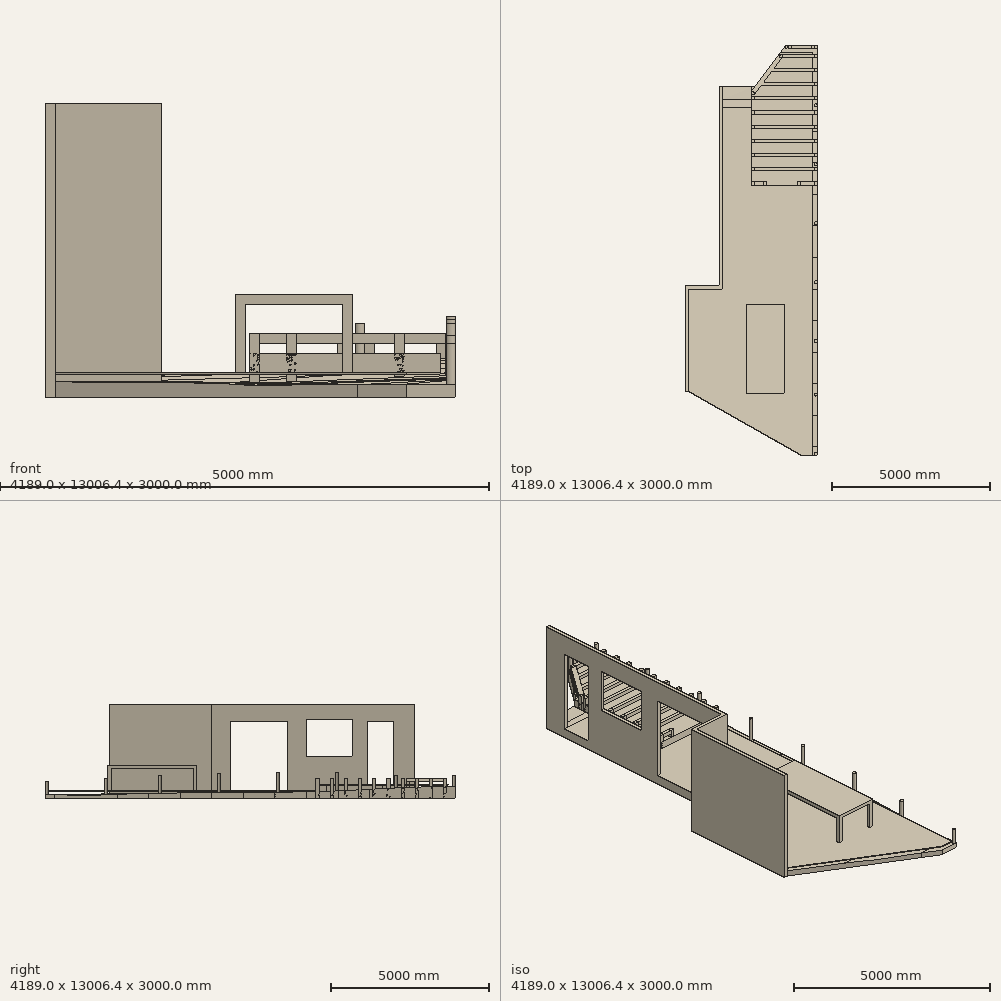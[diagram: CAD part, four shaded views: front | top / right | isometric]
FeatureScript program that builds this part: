
annotation { "Feature Type Name" : "Feature", "Feature Type Description" : "" }
export const myFeature = defineFeature(function(context is Context, id is Id, definition is map)
    precondition{}
    {
        {
            var Q0;
            Q0=qCreatedBy(makeId("Top.planeOp"),FACE);
            var sketch = newSketch(context, id + "F0", { "sketchPlane" : qUnion([Q0])});
            skLineSegment(sketch, "E0", {"start": v(0, 0) * mm, "end": v(0, 6425) * mm});
            skLineSegment(sketch, "E1", {"start": v(0, 0) * mm, "end": v(-1089, 0) * mm});
            skLineSegment(sketch, "E2", {"start": v(-1089, 0) * mm, "end": v(-1089, -3250) * mm});
            skLineSegment(sketch, "E3", {"start": v(-1089, -3250) * mm, "end": v(2495, -5280.43) * mm});
            skLineSegment(sketch, "E4", {"start": v(2495, -5280.43) * mm, "end": v(3000, -5280.43) * mm});
            skLineSegment(sketch, "E5", {"start": v(3000, -5280.43) * mm, "end": v(3000, 7726) * mm});
            skLineSegment(sketch, "E6", {"start": v(0, 6425) * mm, "end": v(1024, 6425) * mm});
            skLineSegment(sketch, "E7", {"start": v(1024, 6425) * mm, "end": v(2000, 7726) * mm});
            skLineSegment(sketch, "E8", {"start": v(2000, 7726) * mm, "end": v(3000, 7726) * mm});
            skPoint(sketch, "E9", {"position": v(1000, 0) * mm});
            skPoint(sketch, "E10", {"position": v(2000, 0) * mm});
            skPoint(sketch, "E11", {"position": v(2000, -1000) * mm});
            skPoint(sketch, "E12", {"position": v(2000, -2000) * mm});
            skPoint(sketch, "E13", {"position": v(2000, -3000) * mm});
            skPoint(sketch, "E14", {"position": v(1000, -1000) * mm});
            skPoint(sketch, "E15", {"position": v(0, -1000) * mm});
            skPoint(sketch, "E16", {"position": v(0, -2000) * mm});
            skPoint(sketch, "E17", {"position": v(1000, -2000) * mm});
            skPoint(sketch, "E18", {"position": v(1000, -3000) * mm});
            skPoint(sketch, "E19", {"position": v(2000, -4000) * mm});
            skPoint(sketch, "E20", {"position": v(1000, 1000) * mm});
            skPoint(sketch, "E21", {"position": v(2000, 1000) * mm});
            skPoint(sketch, "E22", {"position": v(0, 1000) * mm});
            skPoint(sketch, "E23", {"position": v(1000, 2000) * mm});
            skPoint(sketch, "E24", {"position": v(2000, 2000) * mm});
            skPoint(sketch, "E25", {"position": v(1000, 3000) * mm});
            skPoint(sketch, "E26", {"position": v(2000, 3000) * mm});
            skPoint(sketch, "E27", {"position": v(0, 2000) * mm});
            skPoint(sketch, "E28", {"position": v(0, 3000) * mm});
            skPoint(sketch, "E29", {"position": v(1000, 4000) * mm});
            skPoint(sketch, "E30", {"position": v(2000, 4000) * mm});
            skPoint(sketch, "E31", {"position": v(1000, 5000) * mm});
            skPoint(sketch, "E32", {"position": v(2000, 5000) * mm});
            skPoint(sketch, "E33", {"position": v(0, 4000) * mm});
            skPoint(sketch, "E34", {"position": v(0, 5000) * mm});
            skPoint(sketch, "E35", {"position": v(0, 6000) * mm});
            skPoint(sketch, "E36", {"position": v(1000, 6000) * mm});
            skPoint(sketch, "E37", {"position": v(2000, 6000) * mm});
            skPoint(sketch, "E38", {"position": v(-1000, -1000) * mm});
            skPoint(sketch, "E39", {"position": v(-1000, -2000) * mm});
            skPoint(sketch, "E40", {"position": v(-1089, -1000) * mm});
            skPoint(sketch, "E41", {"position": v(-1089, -2000) * mm});
            skPoint(sketch, "E42", {"position": v(-1000, 0) * mm});
            skPoint(sketch, "E43", {"position": v(0, -3000) * mm});
            skPoint(sketch, "E44", {"position": v(-1000, -3000) * mm});
            skPoint(sketch, "E45", {"position": v(-1089, -3000) * mm});
            skPoint(sketch, "E46", {"position": v(1000, -4000) * mm});
            skPoint(sketch, "E47", {"position": v(2000, 7000) * mm});
            skPoint(sketch, "E48", {"position": v(2000, -5000) * mm});
            skPoint(sketch, "E49", {"position": v(-1000, -3300.42) * mm});
            skPoint(sketch, "E50", {"position": v(0, -3866.95) * mm});
            skPoint(sketch, "E51", {"position": v(1000, -4433.47) * mm});
            skPoint(sketch, "E52", {"position": v(3000, -5000) * mm});
            skPoint(sketch, "E53", {"position": v(3000, -4000) * mm});
            skPoint(sketch, "E54", {"position": v(3000, -3000) * mm});
            skPoint(sketch, "E55", {"position": v(3000, -2000) * mm});
            skPoint(sketch, "E56", {"position": v(3000, -1000) * mm});
            skPoint(sketch, "E57", {"position": v(3000, 0) * mm});
            skPoint(sketch, "E58", {"position": v(3000, 1000) * mm});
            skPoint(sketch, "E59", {"position": v(3000, 2000) * mm});
            skPoint(sketch, "E60", {"position": v(3000, 3000) * mm});
            skPoint(sketch, "E61", {"position": v(3000, 4000) * mm});
            skPoint(sketch, "E62", {"position": v(3000, 5000) * mm});
            skPoint(sketch, "E63", {"position": v(3000, 6000) * mm});
            skPoint(sketch, "E64", {"position": v(3000, 7000) * mm});
            skPoint(sketch, "E65", {"position": v(1000, 6425) * mm});
            skPoint(sketch, "E66", {"position": v(2000, -6000) * mm});
            skPoint(sketch, "E67", {"position": v(3000, -6000) * mm});
            skPoint(sketch, "E68", {"position": v(1000, -6000) * mm});
            skPoint(sketch, "E69", {"position": v(0, -6000) * mm});
            skPoint(sketch, "E70", {"position": v(-1000, -6000) * mm});
            skPoint(sketch, "E71", {"position": v(-1089, -6000) * mm});
            skPoint(sketch, "E72", {"position": v(1000, -5000) * mm});
            skPoint(sketch, "E73", {"position": v(0, -5000) * mm});
            skPoint(sketch, "E74", {"position": v(-1000, -5000) * mm});
            skPoint(sketch, "E75", {"position": v(-1089, -5000) * mm});
            skPoint(sketch, "E76", {"position": v(0, -4000) * mm});
            skPoint(sketch, "E77", {"position": v(-1000, -4000) * mm});
            skPoint(sketch, "E78", {"position": v(-1089, -4000) * mm});
            skPoint(sketch, "E79", {"position": v(-1000, 1000) * mm});
            skPoint(sketch, "E80", {"position": v(-1089, 1000) * mm});
            skPoint(sketch, "E81", {"position": v(-1089, 2000) * mm});
            skPoint(sketch, "E82", {"position": v(-1000, 2000) * mm});
            skPoint(sketch, "E83", {"position": v(-1089, 3000) * mm});
            skPoint(sketch, "E84", {"position": v(-1000, 3000) * mm});
            skPoint(sketch, "E85", {"position": v(-1089, 4000) * mm});
            skPoint(sketch, "E86", {"position": v(-1000, 4000) * mm});
            skPoint(sketch, "E87", {"position": v(-1089, 5000) * mm});
            skPoint(sketch, "E88", {"position": v(-1000, 5000) * mm});
            skPoint(sketch, "E89", {"position": v(-1089, 6000) * mm});
            skPoint(sketch, "E90", {"position": v(-1000, 6000) * mm});
            skPoint(sketch, "E91", {"position": v(-1089, 7000) * mm});
            skPoint(sketch, "E92", {"position": v(-1000, 7000) * mm});
            skPoint(sketch, "E93", {"position": v(0, 7000) * mm});
            skPoint(sketch, "E94", {"position": v(0, 8000) * mm});
            skPoint(sketch, "E95", {"position": v(-1000, 8000) * mm});
            skPoint(sketch, "E96", {"position": v(-1089, 8000) * mm});
            skPoint(sketch, "E97", {"position": v(1000, 8000) * mm});
            skPoint(sketch, "E98", {"position": v(2000, 8000) * mm});
            skPoint(sketch, "E99", {"position": v(3000, 8000) * mm});
            skPoint(sketch, "E100", {"position": v(1000, 7000) * mm});
            skSolve(sketch);
        }
        {
            var Q0;
            Q0=qCreatedBy(makeId("Top.planeOp"),FACE);
            cPlane(context, id + "F1", {"entities" : qUnion([Q0]), "cplaneType" : CPlaneType.OFFSET, "offset" : 250 * mm, "oppositeDirection" : true, "width" : 150 * mm, "height" : 150 * mm});
        }
        {
            var Q0;
            Q0=qCreatedBy(id+"F1.planeOp",FACE);
            var sketch = newSketch(context, id + "F2", { "sketchPlane" : qUnion([Q0])});
            skCircle(sketch, "E101", {"center": v(2023.75, 7678.5) * mm, "radius": 47.5 * mm});
            skSolve(sketch);
        }
        {
            var Q0;
            Q0 = qSketchRegion(id + "F2", true);
            extrude(context, id + "F3", {"entities" : qUnion([Q0]), "depth" : 750 * mm, "offsetDistance" : 25 * mm});
        }
        {
            var Q0;
            Q0=qCreatedBy(id+"F1.planeOp",FACE);
            var sketch = newSketch(context, id + "F4", { "sketchPlane" : qUnion([Q0])});
            skCircle(sketch, "E102", {"center": v(2952.5, 7678.5) * mm, "radius": 47.5 * mm});
            skSolve(sketch);
        }
        {
            var Q0;
            Q0 = qSketchRegion(id + "F4", true);
            extrude(context, id + "F5", {"entities" : qUnion([Q0]), "depth" : 750 * mm, "offsetDistance" : 25 * mm});
        }
        {
            var Q0;
            Q0=qCreatedBy(id+"F1.planeOp",FACE);
            var sketch = newSketch(context, id + "F6", { "sketchPlane" : qUnion([Q0])});
            skCircle(sketch, "E103", {"center": v(2952.5, 5831) * mm, "radius": 47.5 * mm});
            skSolve(sketch);
        }
        {
            var Q0;
            Q0 = qSketchRegion(id + "F6", true);
            extrude(context, id + "F7", {"entities" : qUnion([Q0]), "depth" : 750 * mm, "offsetDistance" : 25 * mm});
        }
        {
            var Q0;
            Q0=qCreatedBy(id+"F1.planeOp",FACE);
            var sketch = newSketch(context, id + "F8", { "sketchPlane" : qUnion([Q0])});
            skCircle(sketch, "E104", {"center": v(2952.5, 3956) * mm, "radius": 47.5 * mm});
            skSolve(sketch);
        }
        {
            var Q0;
            Q0 = qSketchRegion(id + "F8", true);
            extrude(context, id + "F9", {"entities" : qUnion([Q0]), "depth" : 820 * mm, "offsetDistance" : 25 * mm});
        }
        {
            var Q0;
            Q0=qCreatedBy(id+"F1.planeOp",FACE);
            var sketch = newSketch(context, id + "F10", { "sketchPlane" : qUnion([Q0])});
            skCircle(sketch, "E105", {"center": v(2952.5, 2092) * mm, "radius": 47.5 * mm});
            skSolve(sketch);
        }
        {
            var Q0;
            Q0 = qSketchRegion(id + "F10", true);
            extrude(context, id + "F11", {"entities" : qUnion([Q0]), "depth" : 830 * mm, "offsetDistance" : 25 * mm});
        }
        {
            var Q0;
            Q0=qCreatedBy(id+"F1.planeOp",FACE);
            var sketch = newSketch(context, id + "F12", { "sketchPlane" : qUnion([Q0])});
            skCircle(sketch, "E106", {"center": v(2952.5, 220) * mm, "radius": 47.5 * mm});
            skSolve(sketch);
        }
        {
            var Q0;
            Q0 = qSketchRegion(id + "F12", true);
            extrude(context, id + "F13", {"entities" : qUnion([Q0]), "depth" : 790 * mm, "offsetDistance" : 25 * mm});
        }
        {
            var Q0;
            Q0=qCreatedBy(id+"F1.planeOp",FACE);
            var sketch = newSketch(context, id + "F14", { "sketchPlane" : qUnion([Q0])});
            skCircle(sketch, "E107", {"center": v(2952.5, -1647) * mm, "radius": 47.5 * mm});
            skSolve(sketch);
        }
        {
            var Q0;
            Q0 = qSketchRegion(id + "F14", true);
            extrude(context, id + "F15", {"entities" : qUnion([Q0]), "depth" : 750 * mm, "offsetDistance" : 25 * mm});
        }
        {
            var Q0;
            Q0=qCreatedBy(id+"F1.planeOp",FACE);
            var sketch = newSketch(context, id + "F16", { "sketchPlane" : qUnion([Q0])});
            skCircle(sketch, "E108", {"center": v(2952.5, -3353) * mm, "radius": 47.5 * mm});
            skSolve(sketch);
        }
        {
            var Q0;
            Q0 = qSketchRegion(id + "F16", true);
            extrude(context, id + "F17", {"entities" : qUnion([Q0]), "depth" : 630 * mm, "offsetDistance" : 25 * mm});
        }
        {
            var Q0;
            Q0=qCreatedBy(id+"F1.planeOp",FACE);
            var sketch = newSketch(context, id + "F18", { "sketchPlane" : qUnion([Q0])});
            skCircle(sketch, "E109", {"center": v(2952.5, -5232.93) * mm, "radius": 47.5 * mm});
            skSolve(sketch);
        }
        {
            var Q0;
            Q0 = qSketchRegion(id + "F18", true);
            extrude(context, id + "F19", {"entities" : qUnion([Q0]), "depth" : 550 * mm, "offsetDistance" : 25 * mm});
        }
        {
            var Q0;
            Q0=sQuery(id+"F0.wireOp",VERTEX,"E94");
            var Q1;
            Q1=qCreatedBy(makeId("Front.planeOp"),FACE);
            cPlane(context, id + "F20", {"entities" : qUnion([Q0, Q1]), "cplaneType" : CPlaneType.PLANE_POINT, "offset" : 25 * mm, "width" : 150 * mm, "height" : 150 * mm});
        }
        {
            var Q0;
            Q0=qCreatedBy(id+"F20.planeOp",FACE);
            var sketch = newSketch(context, id + "F21", { "sketchPlane" : qUnion([Q0])});
            skPoint(sketch, "E110", {"position": v(-1089, -90) * mm});
            skPoint(sketch, "E111", {"position": v(-1000, -90) * mm});
            skPoint(sketch, "E112", {"position": v(0, -1) * mm});
            skPoint(sketch, "E113", {"position": v(1000, 1) * mm});
            skPoint(sketch, "E114", {"position": v(2000, 136) * mm});
            skLineSegment(sketch, "E115", {"start": v(3000, -250) * mm, "end": v(-1089, -250) * mm});
            skLineSegment(sketch, "E116", {"start": v(-1089, -250) * mm, "end": v(-1089, -90) * mm});
            skLineSegment(sketch, "E117", {"start": v(3000, -250) * mm, "end": v(3000, 158) * mm});
            skLineSegment(sketch, "E118", {"start": v(-1089, -90) * mm, "end": v(-1000, -90) * mm});
            skLineSegment(sketch, "E119", {"start": v(-1000, -90) * mm, "end": v(0, -1) * mm});
            skLineSegment(sketch, "E120", {"start": v(0, -1) * mm, "end": v(1000, 1) * mm});
            skFitSpline(sketch, "E121", {"points": [v(3000, 158) * mm, v(2000, 136) * mm, v(1000, 1) * mm], "startDerivative": vector(-253.44, 0) * mm, "endDerivative": vector(-278.02, 0) * mm});
            skSolve(sketch);
        }
        {
            var Q0;
            Q0=sQuery(id+"F0.wireOp",VERTEX,"E93");
            var Q1;
            Q1=qCreatedBy(makeId("Front.planeOp"),FACE);
            cPlane(context, id + "F22", {"entities" : qUnion([Q0, Q1]), "cplaneType" : CPlaneType.PLANE_POINT, "offset" : 25 * mm, "width" : 150 * mm, "height" : 150 * mm});
        }
        {
            var Q0;
            Q0=qCreatedBy(id+"F22.planeOp",FACE);
            var sketch = newSketch(context, id + "F23", { "sketchPlane" : qUnion([Q0])});
            skLineSegment(sketch, "E122", {"start": v(-1089, -90) * mm, "end": v(-1089, -250) * mm});
            skLineSegment(sketch, "E123", {"start": v(-1089, -250) * mm, "end": v(3000, -250) * mm});
            skLineSegment(sketch, "E124", {"start": v(3000, -250) * mm, "end": v(3000, 135) * mm});
            skPoint(sketch, "E125", {"position": v(-1000, -90) * mm});
            skPoint(sketch, "E126", {"position": v(0, -1) * mm});
            skPoint(sketch, "E127", {"position": v(-1000, -2003.57) * mm});
            skPoint(sketch, "E128", {"position": v(1000, 1) * mm});
            skLineSegment(sketch, "E129", {"start": v(-1089, -90) * mm, "end": v(-1000, -90) * mm});
            skLineSegment(sketch, "E130", {"start": v(-1000, -90) * mm, "end": v(0, -1) * mm});
            skLineSegment(sketch, "E131", {"start": v(0, -1) * mm, "end": v(1000, 1) * mm});
            skPoint(sketch, "E132", {"position": v(2000, 87) * mm});
            skFitSpline(sketch, "E133", {"points": [v(3000, 135) * mm, v(2000, 87) * mm, v(1000, 1) * mm], "startDerivative": vector(-235.52, 0) * mm, "endDerivative": vector(-452.7, 6) * mm});
            skSolve(sketch);
        }
        {
            var Q0;
            Q0=qCreatedBy(makeId("Front.planeOp"),FACE);
            var Q1;
            Q1=sQuery(id+"F0.wireOp",VERTEX,"E35");
            cPlane(context, id + "F24", {"entities" : qUnion([Q0, Q1]), "cplaneType" : CPlaneType.PLANE_POINT, "offset" : 25 * mm, "width" : 150 * mm, "height" : 150 * mm});
        }
        {
            var Q0;
            Q0=qCreatedBy(id+"F24.planeOp",FACE);
            var sketch = newSketch(context, id + "F25", { "sketchPlane" : qUnion([Q0])});
            skLineSegment(sketch, "E134", {"start": v(-1089, -90) * mm, "end": v(-1089, -250) * mm});
            skLineSegment(sketch, "E135", {"start": v(-1089, -250) * mm, "end": v(3000, -250) * mm});
            skLineSegment(sketch, "E136", {"start": v(3000, -250) * mm, "end": v(3000, 102) * mm});
            skPoint(sketch, "E137", {"position": v(-1000, -90) * mm});
            skPoint(sketch, "E138", {"position": v(0, -39) * mm});
            skPoint(sketch, "E139", {"position": v(1000, -9) * mm});
            skPoint(sketch, "E140", {"position": v(2000, 38) * mm});
            skLineSegment(sketch, "E141", {"start": v(-1089, -90) * mm, "end": v(-1000, -90) * mm});
            skLineSegment(sketch, "E142", {"start": v(-1000, -90) * mm, "end": v(0, -39) * mm});
            skFitSpline(sketch, "E143", {"points": [v(3000, 102) * mm, v(2000, 38) * mm, v(1000, -9) * mm, v(0, -39) * mm], "startDerivative": vector(-559.95, 0) * mm, "endDerivative": vector(-577.7, 0) * mm});
            skSolve(sketch);
        }
        {
            var Q0;
            Q0=sQuery(id+"F0.wireOp",VERTEX,"E34");
            var Q1;
            Q1=qCreatedBy(makeId("Front.planeOp"),FACE);
            cPlane(context, id + "F26", {"entities" : qUnion([Q0, Q1]), "cplaneType" : CPlaneType.PLANE_POINT, "offset" : 25 * mm, "width" : 150 * mm, "height" : 150 * mm});
        }
        {
            var Q0;
            Q0=qCreatedBy(id+"F26.planeOp",FACE);
            var sketch = newSketch(context, id + "F27", { "sketchPlane" : qUnion([Q0])});
            skLineSegment(sketch, "E144", {"start": v(-1089, -90) * mm, "end": v(-1089, -250) * mm});
            skLineSegment(sketch, "E145", {"start": v(-1089, -250) * mm, "end": v(3000, -250) * mm});
            skLineSegment(sketch, "E146", {"start": v(3000, -250) * mm, "end": v(3000, 50) * mm});
            skLineSegment(sketch, "E147", {"start": v(-1089, -90) * mm, "end": v(-1000, -90) * mm});
            skLineSegment(sketch, "E148", {"start": v(-1000, -90) * mm, "end": v(0, -75) * mm});
            skPoint(sketch, "E149", {"position": v(1000, -51) * mm});
            skPoint(sketch, "E150", {"position": v(2000, -5) * mm});
            skFitSpline(sketch, "E151", {"points": [v(3000, 50) * mm, v(2000, -5) * mm, v(1000, -51) * mm, v(0, -75) * mm], "startDerivative": vector(-368.77, 0) * mm, "endDerivative": vector(-352.57, 0) * mm});
            skSolve(sketch);
        }
        {
            var Q0;
            Q0=sQuery(id+"F0.wireOp",VERTEX,"E33");
            var Q1;
            Q1=qCreatedBy(makeId("Front.planeOp"),FACE);
            cPlane(context, id + "F28", {"entities" : qUnion([Q0, Q1]), "cplaneType" : CPlaneType.PLANE_POINT, "offset" : 25 * mm, "width" : 150 * mm, "height" : 150 * mm});
        }
        {
            var Q0;
            Q0=qCreatedBy(id+"F28.planeOp",FACE);
            var sketch = newSketch(context, id + "F29", { "sketchPlane" : qUnion([Q0])});
            skLineSegment(sketch, "E152", {"start": v(-1089, -90) * mm, "end": v(-1089, -250) * mm});
            skLineSegment(sketch, "E153", {"start": v(-1089, -250) * mm, "end": v(3000, -250) * mm});
            skLineSegment(sketch, "E154", {"start": v(3000, -250) * mm, "end": v(3000, -1) * mm});
            skLineSegment(sketch, "E155", {"start": v(-1089, -90) * mm, "end": v(-1000, -90) * mm});
            skLineSegment(sketch, "E156", {"start": v(-1000, -90) * mm, "end": v(0, -115) * mm});
            skPoint(sketch, "E157", {"position": v(1000, -84) * mm});
            skPoint(sketch, "E158", {"position": v(2000, -11) * mm});
            skFitSpline(sketch, "E159", {"points": [v(3000, -1) * mm, v(2000, -11) * mm, v(1000, -84) * mm, v(0, -115) * mm], "startDerivative": vector(-449.53, 0) * mm, "endDerivative": vector(-406.45, 0) * mm});
            skSolve(sketch);
        }
        {
            var Q0;
            Q0=sQuery(id+"F0.wireOp",VERTEX,"E28");
            var Q1;
            Q1=qCreatedBy(makeId("Front.planeOp"),FACE);
            cPlane(context, id + "F30", {"entities" : qUnion([Q0, Q1]), "cplaneType" : CPlaneType.PLANE_POINT, "offset" : 25 * mm, "width" : 150 * mm, "height" : 150 * mm});
        }
        {
            var Q0;
            Q0=qCreatedBy(id+"F30.planeOp",FACE);
            var sketch = newSketch(context, id + "F31", { "sketchPlane" : qUnion([Q0])});
            skLineSegment(sketch, "E160", {"start": v(0, -116) * mm, "end": v(-1000, -90) * mm});
            skLineSegment(sketch, "E161", {"start": v(-1000, -90) * mm, "end": v(-1089, -90) * mm});
            skLineSegment(sketch, "E162", {"start": v(-1089, -90) * mm, "end": v(-1089, -250) * mm});
            skLineSegment(sketch, "E163", {"start": v(-1089, -250) * mm, "end": v(3000, -250) * mm});
            skLineSegment(sketch, "E164", {"start": v(3000, -250) * mm, "end": v(3000, -26) * mm});
            skPoint(sketch, "E165", {"position": v(1000, -115) * mm});
            skPoint(sketch, "E166", {"position": v(2000, -57) * mm});
            skFitSpline(sketch, "E167", {"points": [v(3000, -26) * mm, v(2000, -57) * mm, v(1000, -115) * mm, v(0, -116) * mm], "startDerivative": vector(-404.01, 0) * mm, "endDerivative": vector(-454.87, 0) * mm});
            skSolve(sketch);
        }
        {
            var Q0;
            Q0=sQuery(id+"F0.wireOp",VERTEX,"E27");
            var Q1;
            Q1=qCreatedBy(makeId("Front.planeOp"),FACE);
            cPlane(context, id + "F32", {"entities" : qUnion([Q0, Q1]), "cplaneType" : CPlaneType.PLANE_POINT, "offset" : 25 * mm, "width" : 150 * mm, "height" : 150 * mm});
        }
        {
            var Q0;
            Q0=qCreatedBy(id+"F32.planeOp",FACE);
            var sketch = newSketch(context, id + "F33", { "sketchPlane" : qUnion([Q0])});
            skLineSegment(sketch, "E168", {"start": v(0, -95) * mm, "end": v(-1000, -90) * mm});
            skLineSegment(sketch, "E169", {"start": v(-1000, -90) * mm, "end": v(-1089, -90) * mm});
            skLineSegment(sketch, "E170", {"start": v(-1089, -90) * mm, "end": v(-1089, -250) * mm});
            skLineSegment(sketch, "E171", {"start": v(-1089, -250) * mm, "end": v(3000, -250) * mm});
            skLineSegment(sketch, "E172", {"start": v(3000, -250) * mm, "end": v(3000, -47) * mm});
            skPoint(sketch, "E173", {"position": v(2000, -85) * mm});
            skPoint(sketch, "E174", {"position": v(1000, -108) * mm});
            skFitSpline(sketch, "E175", {"points": [v(0, -95) * mm, v(1000, -108) * mm, v(2000, -85) * mm, v(3000, -47) * mm], "startDerivative": vector(282.5, 0) * mm, "endDerivative": vector(497.4, 0) * mm});
            skSolve(sketch);
        }
        {
            var Q0;
            Q0=sQuery(id+"F0.wireOp",VERTEX,"E22");
            var Q1;
            Q1=qCreatedBy(makeId("Front.planeOp"),FACE);
            cPlane(context, id + "F34", {"entities" : qUnion([Q0, Q1]), "cplaneType" : CPlaneType.PLANE_POINT, "offset" : 25 * mm, "width" : 150 * mm, "height" : 150 * mm});
        }
        {
            var Q0;
            Q0=qCreatedBy(id+"F34.planeOp",FACE);
            var sketch = newSketch(context, id + "F35", { "sketchPlane" : qUnion([Q0])});
            skLineSegment(sketch, "E176", {"start": v(0, -88) * mm, "end": v(-1000, -90) * mm});
            skLineSegment(sketch, "E177", {"start": v(-1000, -90) * mm, "end": v(-1089, -90) * mm});
            skLineSegment(sketch, "E178", {"start": v(-1089, -90) * mm, "end": v(-1089, -250) * mm});
            skLineSegment(sketch, "E179", {"start": v(-1089, -250) * mm, "end": v(3000, -250) * mm});
            skLineSegment(sketch, "E180", {"start": v(3000, -250) * mm, "end": v(3000, -52) * mm});
            skPoint(sketch, "E181", {"position": v(2000, -101) * mm});
            skPoint(sketch, "E182", {"position": v(1000, -108) * mm});
            skFitSpline(sketch, "E183", {"points": [v(3000, -52) * mm, v(2000, -101) * mm, v(1000, -108) * mm, v(0, -88) * mm], "startDerivative": vector(-444.22, 0) * mm, "endDerivative": vector(-397.4, 0) * mm});
            skSolve(sketch);
        }
        {
            var Q0;
            Q0=qCreatedBy(makeId("Front.planeOp"),FACE);
            var sketch = newSketch(context, id + "F36", { "sketchPlane" : qUnion([Q0])});
            skLineSegment(sketch, "E184", {"start": v(0, -89) * mm, "end": v(-1000, -90) * mm});
            skLineSegment(sketch, "E185", {"start": v(-1000, -90) * mm, "end": v(-1089, -90) * mm});
            skLineSegment(sketch, "E186", {"start": v(-1089, -90) * mm, "end": v(-1089, -250) * mm});
            skLineSegment(sketch, "E187", {"start": v(-1089, -250) * mm, "end": v(3000, -250) * mm});
            skLineSegment(sketch, "E188", {"start": v(3000, -250) * mm, "end": v(3000, -58) * mm});
            skPoint(sketch, "E189", {"position": v(2000, -109) * mm});
            skPoint(sketch, "E190", {"position": v(1000, -105) * mm});
            skFitSpline(sketch, "E191", {"points": [v(0, -89) * mm, v(1000, -105) * mm, v(2000, -109) * mm, v(3000, -58) * mm], "startDerivative": vector(1559.39, 0) * mm, "endDerivative": vector(1883.75, 0) * mm});
            skSolve(sketch);
        }
        {
            var Q0;
            Q0=sQuery(id+"F0.wireOp",VERTEX,"E15");
            var Q1;
            Q1=qCreatedBy(makeId("Front.planeOp"),FACE);
            cPlane(context, id + "F37", {"entities" : qUnion([Q0, Q1]), "cplaneType" : CPlaneType.PLANE_POINT, "offset" : 25 * mm, "width" : 150 * mm, "height" : 150 * mm});
        }
        {
            var Q0;
            Q0=qCreatedBy(id+"F37.planeOp",FACE);
            var sketch = newSketch(context, id + "F38", { "sketchPlane" : qUnion([Q0])});
            skLineSegment(sketch, "E192", {"start": v(-1089, -91) * mm, "end": v(-1089, -250) * mm});
            skLineSegment(sketch, "E193", {"start": v(-1089, -250) * mm, "end": v(3000, -250) * mm});
            skLineSegment(sketch, "E194", {"start": v(3000, -250) * mm, "end": v(3000, -66) * mm});
            skPoint(sketch, "E195", {"position": v(2000, -127) * mm});
            skPoint(sketch, "E196", {"position": v(1000, -112) * mm});
            skPoint(sketch, "E197", {"position": v(0, -97) * mm});
            skPoint(sketch, "E198", {"position": v(-1000, -90) * mm});
            skFitSpline(sketch, "E199", {"points": [v(-1089, -91) * mm, v(-1000, -90) * mm, v(0, -97) * mm, v(1000, -112) * mm, v(2000, -127) * mm, v(3000, -66) * mm], "startDerivative": vector(1882.35, 0) * mm, "endDerivative": vector(2389.42, 0) * mm});
            skSolve(sketch);
        }
        {
            var Q0;
            Q0=sQuery(id+"F0.wireOp",VERTEX,"E16");
            var Q1;
            Q1=qCreatedBy(makeId("Front.planeOp"),FACE);
            cPlane(context, id + "F39", {"entities" : qUnion([Q0, Q1]), "cplaneType" : CPlaneType.PLANE_POINT, "offset" : 25 * mm, "width" : 150 * mm, "height" : 150 * mm});
        }
        {
            var Q0;
            Q0=qCreatedBy(id+"F39.planeOp",FACE);
            var sketch = newSketch(context, id + "F40", { "sketchPlane" : qUnion([Q0])});
            skLineSegment(sketch, "E200", {"start": v(-1089, -87) * mm, "end": v(-1089, -250) * mm});
            skLineSegment(sketch, "E201", {"start": v(-1089, -250) * mm, "end": v(3000, -250) * mm});
            skLineSegment(sketch, "E202", {"start": v(3000, -250) * mm, "end": v(3000, -72) * mm});
            skPoint(sketch, "E203", {"position": v(2000, -150) * mm});
            skPoint(sketch, "E204", {"position": v(1000, -116) * mm});
            skPoint(sketch, "E205", {"position": v(0, -99) * mm});
            skPoint(sketch, "E206", {"position": v(-1000, -86) * mm});
            skFitSpline(sketch, "E207", {"points": [v(-1089, -87) * mm, v(-1000, -86) * mm, v(0, -99) * mm, v(1000, -116) * mm, v(2000, -150) * mm, v(3000, -72) * mm], "startDerivative": vector(1438.85, 0) * mm, "endDerivative": vector(1028.07, 0) * mm});
            skSolve(sketch);
        }
        {
            var Q0;
            Q0=sQuery(id+"F0.wireOp",VERTEX,"E43");
            var Q1;
            Q1=qCreatedBy(makeId("Front.planeOp"),FACE);
            cPlane(context, id + "F41", {"entities" : qUnion([Q0, Q1]), "cplaneType" : CPlaneType.PLANE_POINT, "offset" : 25 * mm, "width" : 150 * mm, "height" : 150 * mm});
        }
        {
            var Q0;
            Q0=qCreatedBy(id+"F41.planeOp",FACE);
            var sketch = newSketch(context, id + "F42", { "sketchPlane" : qUnion([Q0])});
            skLineSegment(sketch, "E208", {"start": v(-1089, -86) * mm, "end": v(-1089, -250) * mm});
            skLineSegment(sketch, "E209", {"start": v(-1089, -250) * mm, "end": v(3000, -250) * mm});
            skLineSegment(sketch, "E210", {"start": v(3000, -250) * mm, "end": v(3000, -110) * mm});
            skPoint(sketch, "E211", {"position": v(2000, -181) * mm});
            skPoint(sketch, "E212", {"position": v(1000, -115) * mm});
            skPoint(sketch, "E213", {"position": v(0, -95) * mm});
            skPoint(sketch, "E214", {"position": v(-1000, -86) * mm});
            skFitSpline(sketch, "E215", {"points": [v(-1089, -86) * mm, v(-1000, -86) * mm, v(0, -95) * mm, v(1000, -115) * mm, v(2000, -181) * mm, v(3000, -110) * mm], "startDerivative": vector(1010.72, 0) * mm, "endDerivative": vector(215.3, 0) * mm});
            skSolve(sketch);
        }
        {
            var Q0;
            Q0=sQuery(id+"F0.wireOp",VERTEX,"E76");
            var Q1;
            Q1=qCreatedBy(makeId("Front.planeOp"),FACE);
            cPlane(context, id + "F43", {"entities" : qUnion([Q0, Q1]), "cplaneType" : CPlaneType.PLANE_POINT, "offset" : 25 * mm, "width" : 150 * mm, "height" : 150 * mm});
        }
        {
            var Q0;
            Q0=qCreatedBy(id+"F43.planeOp",FACE);
            var sketch = newSketch(context, id + "F44", { "sketchPlane" : qUnion([Q0])});
            skLineSegment(sketch, "E216", {"start": v(-1089, -98) * mm, "end": v(-1089, -250) * mm});
            skLineSegment(sketch, "E217", {"start": v(-1089, -250) * mm, "end": v(3000, -250) * mm});
            skLineSegment(sketch, "E218", {"start": v(3000, -250) * mm, "end": v(3000, -149) * mm});
            skPoint(sketch, "E219", {"position": v(2000, -164) * mm});
            skPoint(sketch, "E220", {"position": v(1000, -116) * mm});
            skPoint(sketch, "E221", {"position": v(0, -102) * mm});
            skPoint(sketch, "E222", {"position": v(-1000, -104) * mm});
            skFitSpline(sketch, "E223", {"points": [v(-1089, -98) * mm, v(-1000, -104) * mm, v(0, -102) * mm, v(1000, -116) * mm, v(2000, -164) * mm, v(3000, -149) * mm], "startDerivative": vector(771.3, 0) * mm, "endDerivative": vector(796.92, 0) * mm});
            skSolve(sketch);
        }
        {
            var Q0;
            Q0=sQuery(id+"F0.wireOp",VERTEX,"E73");
            var Q1;
            Q1=qCreatedBy(makeId("Front.planeOp"),FACE);
            cPlane(context, id + "F45", {"entities" : qUnion([Q0, Q1]), "cplaneType" : CPlaneType.PLANE_POINT, "offset" : 25 * mm, "width" : 150 * mm, "height" : 150 * mm});
        }
        {
            var Q0;
            Q0=qCreatedBy(id+"F45.planeOp",FACE);
            var sketch = newSketch(context, id + "F46", { "sketchPlane" : qUnion([Q0])});
            skLineSegment(sketch, "E224", {"start": v(-1089, -98) * mm, "end": v(-1089, -250) * mm});
            skLineSegment(sketch, "E225", {"start": v(-1089, -250) * mm, "end": v(3000, -250) * mm});
            skLineSegment(sketch, "E226", {"start": v(3000, -250) * mm, "end": v(3000, -116) * mm});
            skLineSegment(sketch, "E227", {"start": v(-1089, -98) * mm, "end": v(-1000, -104) * mm});
            skLineSegment(sketch, "E228", {"start": v(-1000, -104) * mm, "end": v(0, -102) * mm});
            skPoint(sketch, "E229", {"position": v(1000, -100) * mm});
            skPoint(sketch, "E230", {"position": v(2000, -114) * mm});
            skFitSpline(sketch, "E231", {"points": [v(3000, -116) * mm, v(2000, -114) * mm, v(1000, -100) * mm, v(0, -102) * mm], "startDerivative": vector(-644.69, 0) * mm, "endDerivative": vector(-451.06, 0) * mm});
            skSolve(sketch);
        }
        {
            var Q0;
            Q0=sQuery(id+"F0.wireOp",VERTEX,"E69");
            var Q1;
            Q1=qCreatedBy(makeId("Front.planeOp"),FACE);
            cPlane(context, id + "F47", {"entities" : qUnion([Q0, Q1]), "cplaneType" : CPlaneType.PLANE_POINT, "offset" : 25 * mm, "width" : 150 * mm, "height" : 150 * mm});
        }
        {
            var Q0;
            Q0=qCreatedBy(id+"F47.planeOp",FACE);
            var sketch = newSketch(context, id + "F48", { "sketchPlane" : qUnion([Q0])});
            skLineSegment(sketch, "E232", {"start": v(0, -102) * mm, "end": v(-1000, -104) * mm});
            skLineSegment(sketch, "E233", {"start": v(-1000, -104) * mm, "end": v(-1089, -98) * mm});
            skLineSegment(sketch, "E234", {"start": v(-1089, -98) * mm, "end": v(-1089, -250) * mm});
            skLineSegment(sketch, "E235", {"start": v(-1089, -250) * mm, "end": v(3000, -250) * mm});
            skLineSegment(sketch, "E236", {"start": v(3000, -250) * mm, "end": v(3000, -116) * mm});
            skPoint(sketch, "E237", {"position": v(2000, -114) * mm});
            skPoint(sketch, "E238", {"position": v(1000, -100) * mm});
            skFitSpline(sketch, "E239", {"points": [v(0, -102) * mm, v(1000, -100) * mm, v(2000, -114) * mm, v(3000, -116) * mm], "startDerivative": vector(642.39, 0) * mm, "endDerivative": vector(312.96, 0) * mm});
            skSolve(sketch);
        }
        {
            var Q0;
            Q0 = qSketchRegion(id + "F21", true);
            var Q1;
            Q1 = qSketchRegion(id + "F23", true);
            loft(context, id + "F49", {"sheetProfilesArray" : [{ "sheetProfileEntities" : qUnion([Q0]) }, { "sheetProfileEntities" : qUnion([Q1]) }]});
        }
        {
            var Q0;
            Q0 = qSketchRegion(id + "F25", true);
            var Q1;
            Q1 = qSketchRegion(id + "F23", true);
            loft(context, id + "F50", {"sheetProfilesArray" : [{ "sheetProfileEntities" : qUnion([Q0]) }, { "sheetProfileEntities" : qUnion([Q1]) }]});
        }
        {
            var Q0;
            Q0 = qSketchRegion(id + "F25", true);
            var Q1;
            Q1 = qSketchRegion(id + "F27", true);
            loft(context, id + "F51", {"sheetProfilesArray" : [{ "sheetProfileEntities" : qUnion([Q0]) }, { "sheetProfileEntities" : qUnion([Q1]) }]});
        }
        {
            var Q0;
            Q0 = qSketchRegion(id + "F27", true);
            var Q1;
            Q1 = qSketchRegion(id + "F29", true);
            loft(context, id + "F52", {"sheetProfilesArray" : [{ "sheetProfileEntities" : qUnion([Q0]) }, { "sheetProfileEntities" : qUnion([Q1]) }]});
        }
        {
            var Q0;
            Q0 = qSketchRegion(id + "F29", true);
            var Q1;
            Q1 = qSketchRegion(id + "F31", true);
            loft(context, id + "F53", {"sheetProfilesArray" : [{ "sheetProfileEntities" : qUnion([Q0]) }, { "sheetProfileEntities" : qUnion([Q1]) }]});
        }
        {
            var Q0;
            Q0 = qSketchRegion(id + "F31", true);
            var Q1;
            Q1 = qSketchRegion(id + "F33", true);
            loft(context, id + "F54", {"sheetProfilesArray" : [{ "sheetProfileEntities" : qUnion([Q0]) }, { "sheetProfileEntities" : qUnion([Q1]) }]});
        }
        {
            var Q0;
            Q0 = qSketchRegion(id + "F33", true);
            var Q1;
            Q1 = qSketchRegion(id + "F35", true);
            loft(context, id + "F55", {"sheetProfilesArray" : [{ "sheetProfileEntities" : qUnion([Q0]) }, { "sheetProfileEntities" : qUnion([Q1]) }]});
        }
        {
            var Q0;
            Q0 = qSketchRegion(id + "F35", true);
            var Q1;
            Q1 = qSketchRegion(id + "F36", true);
            loft(context, id + "F56", {"sheetProfilesArray" : [{ "sheetProfileEntities" : qUnion([Q0]) }, { "sheetProfileEntities" : qUnion([Q1]) }]});
        }
        {
            var Q0;
            Q0 = qSketchRegion(id + "F38", true);
            var Q1;
            Q1 = qSketchRegion(id + "F36", true);
            loft(context, id + "F57", {"sheetProfilesArray" : [{ "sheetProfileEntities" : qUnion([Q0]) }, { "sheetProfileEntities" : qUnion([Q1]) }]});
        }
        {
            var Q0;
            Q0 = qSketchRegion(id + "F38", true);
            var Q1;
            Q1 = qSketchRegion(id + "F40", true);
            loft(context, id + "F58", {"sheetProfilesArray" : [{ "sheetProfileEntities" : qUnion([Q0]) }, { "sheetProfileEntities" : qUnion([Q1]) }]});
        }
        {
            var Q0;
            Q0 = qSketchRegion(id + "F40", true);
            var Q1;
            Q1 = qSketchRegion(id + "F42", true);
            loft(context, id + "F59", {"sheetProfilesArray" : [{ "sheetProfileEntities" : qUnion([Q0]) }, { "sheetProfileEntities" : qUnion([Q1]) }]});
        }
        {
            var Q0;
            Q0 = qSketchRegion(id + "F42", true);
            var Q1;
            Q1 = qSketchRegion(id + "F44", true);
            loft(context, id + "F60", {"sheetProfilesArray" : [{ "sheetProfileEntities" : qUnion([Q0]) }, { "sheetProfileEntities" : qUnion([Q1]) }]});
        }
        {
            var Q1;
            Q1 = qSketchRegion(id + "F46", true);
            var Q2;
            Q2 = qSketchRegion(id + "F44", true);
            loft(context, id + "F61", {"operationType" : NewBodyOperationType.ADD, "sheetProfilesArray" : [{ "sheetProfileEntities" : qUnion([Q1]) }, { "sheetProfileEntities" : qUnion([Q2]) }]});
        }
        {
            var Q0;
            Q0 = qSketchRegion(id + "F46", true);
            var Q1;
            Q1 = qSketchRegion(id + "F48", true);
            loft(context, id + "F62", {"sheetProfilesArray" : [{ "sheetProfileEntities" : qUnion([Q0]) }, { "sheetProfileEntities" : qUnion([Q1]) }]});
        }
        {
            var Q0;
            Q0=qCreatedBy(id+"F1.planeOp",FACE);
            var sketch = newSketch(context, id + "F63", { "sketchPlane" : qUnion([Q0])});
            skLineSegment(sketch, "E240", {"start": v(3000, 8000) * mm, "end": v(3000, 7726) * mm});
            skLineSegment(sketch, "E241", {"start": v(3000, 7726) * mm, "end": v(2000, 7726) * mm});
            skLineSegment(sketch, "E242", {"start": v(2000, 7726) * mm, "end": v(1024, 6425) * mm});
            skLineSegment(sketch, "E243", {"start": v(1024, 6425) * mm, "end": v(0, 6425) * mm});
            skLineSegment(sketch, "E244", {"start": v(0, 6425) * mm, "end": v(0, 0) * mm});
            skLineSegment(sketch, "E245", {"start": v(0, 0) * mm, "end": v(-1089, 0) * mm});
            skLineSegment(sketch, "E246", {"start": v(-1089, -3250) * mm, "end": v(2495, -5280.43) * mm});
            skLineSegment(sketch, "E247", {"start": v(2495, -5280.43) * mm, "end": v(3000, -5280.43) * mm});
            skLineSegment(sketch, "E248", {"start": v(3000, -5280.43) * mm, "end": v(3000, -6000) * mm});
            skLineSegment(sketch, "E249", {"start": v(3000, -6000) * mm, "end": v(-1089, -6000) * mm});
            skLineSegment(sketch, "E250", {"start": v(-1089, 0) * mm, "end": v(-1089, 8000) * mm});
            skLineSegment(sketch, "E251", {"start": v(-1089, 8000) * mm, "end": v(3000, 8000) * mm});
            skLineSegment(sketch, "E252", {"start": v(-1089, -3250) * mm, "end": v(-1089, -6000) * mm});
            skSolve(sketch);
        }
        {
            var Q0;
            Q0 = qSketchRegion(id + "F63", true);
            extrude(context, id + "F64", {"entities" : qUnion([Q0]), "operationType" : NewBodyOperationType.REMOVE, "endBound" : BoundingType.THROUGH_ALL, "depth" : 25 * mm, "offsetDistance" : 25 * mm});
        }
        {
            var Q0;
            Q0=qCreatedBy(id+"F1.planeOp",FACE);
            var sketch = newSketch(context, id + "F65", { "sketchPlane" : qUnion([Q0])});
            skLineSegment(sketch, "E253", {"start": v(0, 0) * mm, "end": v(0, 6425) * mm});
            skLineSegment(sketch, "E254", {"start": v(0, 6425) * mm, "end": v(-100, 6425) * mm});
            skLineSegment(sketch, "E255", {"start": v(-100, 6425) * mm, "end": v(-100, 100) * mm});
            skLineSegment(sketch, "E256", {"start": v(-100, 100) * mm, "end": v(-1189, 100) * mm});
            skLineSegment(sketch, "E257", {"start": v(-1189, 100) * mm, "end": v(-1189, -3250) * mm});
            skLineSegment(sketch, "E258", {"start": v(-1189, -3250) * mm, "end": v(-1089, -3250) * mm});
            skLineSegment(sketch, "E259", {"start": v(-1089, -3250) * mm, "end": v(-1089, 0) * mm});
            skLineSegment(sketch, "E260", {"start": v(-1089, 0) * mm, "end": v(0, 0) * mm});
            skSolve(sketch);
        }
        {
            var Q0;
            Q0 = qSketchRegion(id + "F65", true);
            extrude(context, id + "F66", {"entities" : qUnion([Q0]), "depth" : 3000 * mm, "offsetDistance" : 25 * mm});
        }
        {
            assignVariable(context, id + "F67", {"name" : "PaverThickness", "anyValue" : 40});
        }
        {
            var Q0;
            Q0=qCreatedBy(makeId("Top.planeOp"),FACE);
            cPlane(context, id + "F68", {"entities" : qUnion([Q0]), "cplaneType" : CPlaneType.OFFSET, "offset" : (getVariable(context, 'PaverThickness')) * mm, "oppositeDirection" : true, "width" : 150 * mm, "height" : 150 * mm});
        }
        {
            var Q0;
            Q0=makeQuery(id+"F66.opExtrude","SWEPT_FACE",FACE,{"disambiguationData":[OSD([sQuery(id+"F65.wireOp",EDGE,"E253")])]});
            var sketch = newSketch(context, id + "F69", { "sketchPlane" : qUnion([Q0])});
            skLineSegment(sketch, "E261.bottom", {"start": v(600, 0) * mm, "end": v(2400, 0) * mm});
            skLineSegment(sketch, "E261.top", {"start": v(600, 2200) * mm, "end": v(2400, 2200) * mm});
            skLineSegment(sketch, "E261.left", {"start": v(600, 0) * mm, "end": v(600, 2200) * mm});
            skLineSegment(sketch, "E261.right", {"start": v(2400, 0) * mm, "end": v(2400, 2200) * mm});
            skSolve(sketch);
        }
        {
            var Q0;
            Q0 = qSketchRegion(id + "F69", true);
            extrude(context, id + "F70", {"entities" : qUnion([Q0]), "operationType" : NewBodyOperationType.REMOVE, "oppositeDirection" : true, "depth" : 100 * mm, "offsetDistance" : 25 * mm});
        }
        {
            var Q0;
            Q0=makeQuery(id+"F66.opExtrude","SWEPT_FACE",FACE,{"disambiguationData":[OSD([sQuery(id+"F65.wireOp",EDGE,"E253")])]});
            var sketch = newSketch(context, id + "F71", { "sketchPlane" : qUnion([Q0])});
            skLineSegment(sketch, "E262.bottom", {"start": v(3000, 2250) * mm, "end": v(4450, 2250) * mm});
            skLineSegment(sketch, "E262.top", {"start": v(3000, 1100) * mm, "end": v(4450, 1100) * mm});
            skLineSegment(sketch, "E262.left", {"start": v(3000, 2250) * mm, "end": v(3000, 1100) * mm});
            skLineSegment(sketch, "E262.right", {"start": v(4450, 2250) * mm, "end": v(4450, 1100) * mm});
            skSolve(sketch);
        }
        {
            var Q0;
            Q0 = qSketchRegion(id + "F71", true);
            extrude(context, id + "F72", {"entities" : qUnion([Q0]), "operationType" : NewBodyOperationType.REMOVE, "oppositeDirection" : true, "depth" : 100 * mm, "offsetDistance" : 25 * mm});
        }
        {
            var Q0;
            Q0=makeQuery(id+"F66.opExtrude","SWEPT_FACE",FACE,{"disambiguationData":[OSD([sQuery(id+"F65.wireOp",EDGE,"E253")])]});
            var sketch = newSketch(context, id + "F73", { "sketchPlane" : qUnion([Q0])});
            skLineSegment(sketch, "E263.bottom", {"start": v(4920, 2200) * mm, "end": v(5770, 2200) * mm});
            skLineSegment(sketch, "E263.top", {"start": v(4920, 0) * mm, "end": v(5770, 0) * mm});
            skLineSegment(sketch, "E263.left", {"start": v(4920, 2200) * mm, "end": v(4920, 0) * mm});
            skLineSegment(sketch, "E263.right", {"start": v(5770, 2200) * mm, "end": v(5770, 0) * mm});
            skSolve(sketch);
        }
        {
            var Q0;
            Q0 = qSketchRegion(id + "F73", true);
            extrude(context, id + "F74", {"entities" : qUnion([Q0]), "operationType" : NewBodyOperationType.REMOVE, "oppositeDirection" : true, "depth" : 100 * mm, "offsetDistance" : 25 * mm});
        }
        {
            var Q0;
            Q0=qCreatedBy(makeId("Top.planeOp"),FACE);
            cPlane(context, id + "F75", {"entities" : qUnion([Q0]), "cplaneType" : CPlaneType.OFFSET, "offset" : 20 * mm, "oppositeDirection" : true, "width" : 150 * mm, "height" : 150 * mm});
        }
        {
            var Q0;
            Q0=qCreatedBy(makeId("Top.planeOp"),FACE);
            var sketch = newSketch(context, id + "F76", { "sketchPlane" : qUnion([Q0])});
            skLineSegment(sketch, "E264", {"start": v(0, 5770) * mm, "end": v(850, 5770) * mm});
            skArc(sketch, "E265", {"start": v(850, 5770) * mm, "mid": v(601.04, 5168.96) * mm, "end": v(0, 4920) * mm});
            skSolve(sketch);
        }
        {
            var Q0;
            Q0=qCreatedBy(makeId("Top.planeOp"),FACE);
            var sketch = newSketch(context, id + "F77", { "sketchPlane" : qUnion([Q0])});
            skLineSegment(sketch, "E266", {"start": v(300, -4036.9) * mm, "end": v(300, 6425) * mm});
            skLineSegment(sketch, "E267", {"start": v(2850, 3300) * mm, "end": v(2850, -5280.43) * mm});
            skLineSegment(sketch, "E268", {"start": v(0, 0) * mm, "end": v(0, -3866.95) * mm});
            skLineSegment(sketch, "E269", {"start": v(-300, 0) * mm, "end": v(-300, -3696.99) * mm});
            skLineSegment(sketch, "E270", {"start": v(-600, 0) * mm, "end": v(-600, -3527.03) * mm});
            skLineSegment(sketch, "E271", {"start": v(-900, 0) * mm, "end": v(-900, -3357.07) * mm});
            skLineSegment(sketch, "E272", {"start": v(0, 0) * mm, "end": v(300, 0) * mm});
            skLineSegment(sketch, "E273.trimOffspring", {"start": v(600, 0) * mm, "end": v(900, 0) * mm});
            skLineSegment(sketch, "E274.trimOffspring", {"start": v(1200, 0) * mm, "end": v(1500, 0) * mm});
            skLineSegment(sketch, "E275.trimOffspring", {"start": v(1800, 0) * mm, "end": v(2100, 0) * mm});
            skLineSegment(sketch, "E276.trimOffspring", {"start": v(2400, 0) * mm, "end": v(2700, 0) * mm});
            skLineSegment(sketch, "E277", {"start": v(300, 300) * mm, "end": v(600, 300) * mm});
            skPoint(sketch, "E278.orphan", {"position": v(0, 300) * mm});
            skLineSegment(sketch, "E279.trimOffspring", {"start": v(900, 300) * mm, "end": v(1200, 300) * mm});
            skLineSegment(sketch, "E280.trimOffspring", {"start": v(1500, 300) * mm, "end": v(1800, 300) * mm});
            skLineSegment(sketch, "E281.trimOffspring", {"start": v(2100, 300) * mm, "end": v(2400, 300) * mm});
            skLineSegment(sketch, "E282.trimOffspring", {"start": v(2700, 300) * mm, "end": v(2850, 300) * mm});
            skLineSegment(sketch, "E283", {"start": v(0, 600) * mm, "end": v(300, 600) * mm});
            skLineSegment(sketch, "E284", {"start": v(300, 900) * mm, "end": v(600, 900) * mm});
            skLineSegment(sketch, "E285", {"start": v(0, 1200) * mm, "end": v(300, 1200) * mm});
            skLineSegment(sketch, "E286", {"start": v(300, 1500) * mm, "end": v(600, 1500) * mm});
            skLineSegment(sketch, "E287", {"start": v(0, 1800) * mm, "end": v(300, 1800) * mm});
            skLineSegment(sketch, "E288", {"start": v(300, 2100) * mm, "end": v(600, 2100) * mm});
            skLineSegment(sketch, "E289", {"start": v(0, 2400) * mm, "end": v(300, 2400) * mm});
            skLineSegment(sketch, "E290", {"start": v(300, 2700) * mm, "end": v(600, 2700) * mm});
            skLineSegment(sketch, "E291", {"start": v(0, 3000) * mm, "end": v(300, 3000) * mm});
            skLineSegment(sketch, "E292.trimOffspring", {"start": v(600, 600) * mm, "end": v(900, 600) * mm});
            skLineSegment(sketch, "E293.trimOffspring", {"start": v(1200, 600) * mm, "end": v(1500, 600) * mm});
            skLineSegment(sketch, "E294.trimOffspring", {"start": v(1800, 600) * mm, "end": v(2100, 600) * mm});
            skLineSegment(sketch, "E295.trimOffspring", {"start": v(2400, 600) * mm, "end": v(2700, 600) * mm});
            skPoint(sketch, "E296.orphan", {"position": v(0, 900) * mm});
            skLineSegment(sketch, "E297.trimOffspring", {"start": v(900, 900) * mm, "end": v(1200, 900) * mm});
            skLineSegment(sketch, "E298.trimOffspring", {"start": v(1500, 900) * mm, "end": v(1800, 900) * mm});
            skLineSegment(sketch, "E299.trimOffspring", {"start": v(2100, 900) * mm, "end": v(2400, 900) * mm});
            skLineSegment(sketch, "E300.trimOffspring", {"start": v(2700, 900) * mm, "end": v(2850, 900) * mm});
            skLineSegment(sketch, "E301.trimOffspring", {"start": v(600, 1200) * mm, "end": v(900, 1200) * mm});
            skLineSegment(sketch, "E302.trimOffspring", {"start": v(1200, 1200) * mm, "end": v(1500, 1200) * mm});
            skLineSegment(sketch, "E303.trimOffspring", {"start": v(1800, 1200) * mm, "end": v(2100, 1200) * mm});
            skLineSegment(sketch, "E304.trimOffspring", {"start": v(2400, 1200) * mm, "end": v(2700, 1200) * mm});
            skPoint(sketch, "E305.orphan", {"position": v(0, 1500) * mm});
            skLineSegment(sketch, "E306.trimOffspring", {"start": v(900, 1500) * mm, "end": v(1200, 1500) * mm});
            skLineSegment(sketch, "E307.trimOffspring", {"start": v(1500, 1500) * mm, "end": v(1800, 1500) * mm});
            skLineSegment(sketch, "E308.trimOffspring", {"start": v(2100, 1500) * mm, "end": v(2400, 1500) * mm});
            skLineSegment(sketch, "E309.trimOffspring", {"start": v(2700, 1500) * mm, "end": v(2850, 1500) * mm});
            skLineSegment(sketch, "E310.trimOffspring", {"start": v(600, 1800) * mm, "end": v(900, 1800) * mm});
            skLineSegment(sketch, "E311.trimOffspring", {"start": v(1200, 1800) * mm, "end": v(1500, 1800) * mm});
            skLineSegment(sketch, "E312.trimOffspring", {"start": v(1800, 1800) * mm, "end": v(2100, 1800) * mm});
            skLineSegment(sketch, "E313.trimOffspring", {"start": v(2400, 1800) * mm, "end": v(2700, 1800) * mm});
            skPoint(sketch, "E314.orphan", {"position": v(0, 2100) * mm});
            skLineSegment(sketch, "E315.trimOffspring", {"start": v(900, 2100) * mm, "end": v(1200, 2100) * mm});
            skLineSegment(sketch, "E316.trimOffspring", {"start": v(1500, 2100) * mm, "end": v(1800, 2100) * mm});
            skLineSegment(sketch, "E317.trimOffspring", {"start": v(2100, 2100) * mm, "end": v(2400, 2100) * mm});
            skLineSegment(sketch, "E318.trimOffspring", {"start": v(2700, 2100) * mm, "end": v(2850, 2100) * mm});
            skLineSegment(sketch, "E319.trimOffspring", {"start": v(600, 2400) * mm, "end": v(900, 2400) * mm});
            skLineSegment(sketch, "E320.trimOffspring", {"start": v(1200, 2400) * mm, "end": v(1500, 2400) * mm});
            skLineSegment(sketch, "E321.trimOffspring", {"start": v(1800, 2400) * mm, "end": v(2100, 2400) * mm});
            skLineSegment(sketch, "E322.trimOffspring", {"start": v(2400, 2400) * mm, "end": v(2700, 2400) * mm});
            skPoint(sketch, "E323.orphan", {"position": v(0, 2700) * mm});
            skLineSegment(sketch, "E324.trimOffspring", {"start": v(900, 2700) * mm, "end": v(1200, 2700) * mm});
            skLineSegment(sketch, "E325.trimOffspring", {"start": v(1500, 2700) * mm, "end": v(1800, 2700) * mm});
            skLineSegment(sketch, "E326.trimOffspring", {"start": v(2100, 2700) * mm, "end": v(2400, 2700) * mm});
            skLineSegment(sketch, "E327.trimOffspring", {"start": v(2700, 2700) * mm, "end": v(2850, 2700) * mm});
            skLineSegment(sketch, "E328", {"start": v(300, 3300) * mm, "end": v(600, 3300) * mm});
            skLineSegment(sketch, "E329", {"start": v(0, 3600) * mm, "end": v(300, 3600) * mm});
            skLineSegment(sketch, "E330", {"start": v(300, 3900) * mm, "end": v(600, 3900) * mm});
            skLineSegment(sketch, "E331", {"start": v(0, 4200) * mm, "end": v(300, 4200) * mm});
            skLineSegment(sketch, "E332", {"start": v(300, 4500) * mm, "end": v(600, 4500) * mm});
            skLineSegment(sketch, "E333.trimOffspring", {"start": v(600, 3000) * mm, "end": v(900, 3000) * mm});
            skLineSegment(sketch, "E334.trimOffspring", {"start": v(1200, 3000) * mm, "end": v(1500, 3000) * mm});
            skLineSegment(sketch, "E335.trimOffspring", {"start": v(1800, 3000) * mm, "end": v(2100, 3000) * mm});
            skLineSegment(sketch, "E336.trimOffspring", {"start": v(2400, 3000) * mm, "end": v(2700, 3000) * mm});
            skPoint(sketch, "E337.orphan", {"position": v(0, 3300) * mm});
            skLineSegment(sketch, "E338.trimOffspring", {"start": v(900, 3300) * mm, "end": v(1200, 3300) * mm});
            skLineSegment(sketch, "E339.trimOffspring", {"start": v(1500, 3300) * mm, "end": v(1800, 3300) * mm});
            skLineSegment(sketch, "E340.trimOffspring", {"start": v(2100, 3300) * mm, "end": v(2400, 3300) * mm});
            skLineSegment(sketch, "E341.trimOffspring", {"start": v(2700, 3300) * mm, "end": v(2850, 3300) * mm});
            skLineSegment(sketch, "E342.trimOffspring", {"start": v(600, 3600) * mm, "end": v(900, 3600) * mm});
            skLineSegment(sketch, "E343.trimOffspring", {"start": v(1200, 3600) * mm, "end": v(1500, 3600) * mm});
            skLineSegment(sketch, "E344.trimOffspring", {"start": v(1800, 3600) * mm, "end": v(2100, 3600) * mm});
            skPoint(sketch, "E345.orphan", {"position": v(0, 3900) * mm});
            skLineSegment(sketch, "E346.trimOffspring", {"start": v(900, 3900) * mm, "end": v(1200, 3900) * mm});
            skLineSegment(sketch, "E347.trimOffspring", {"start": v(1500, 3900) * mm, "end": v(1800, 3900) * mm});
            skLineSegment(sketch, "E348.trimOffspring", {"start": v(600, 4200) * mm, "end": v(900, 4200) * mm});
            skLineSegment(sketch, "E349.trimOffspring", {"start": v(1200, 4200) * mm, "end": v(1500, 4200) * mm});
            skLineSegment(sketch, "E350.trimOffspring", {"start": v(2700, 3300) * mm, "end": v(2700, -5280.43) * mm});
            skLineSegment(sketch, "E351.trimOffspring", {"start": v(2400, 3300) * mm, "end": v(2400, -5226.61) * mm});
            skLineSegment(sketch, "E352.trimOffspring", {"start": v(2100, 3600) * mm, "end": v(2100, -5056.65) * mm});
            skLineSegment(sketch, "E353.trimOffspring", {"start": v(1800, 3900) * mm, "end": v(1800, -4886.7) * mm});
            skLineSegment(sketch, "E354", {"start": v(0, 4800) * mm, "end": v(300, 4800) * mm});
            skLineSegment(sketch, "E355", {"start": v(300, 5100) * mm, "end": v(600, 5100) * mm});
            skPoint(sketch, "E356.orphan", {"position": v(0, 4500) * mm});
            skLineSegment(sketch, "E357.trimOffspring", {"start": v(900, 4500) * mm, "end": v(1200, 4500) * mm});
            skLineSegment(sketch, "E358.trimOffspring", {"start": v(600, 4800) * mm, "end": v(900, 4800) * mm});
            skLineSegment(sketch, "E359.trimOffspring", {"start": v(1200, 4800) * mm, "end": v(1500, 4800) * mm});
            skPoint(sketch, "E360.orphan", {"position": v(0, 5100) * mm});
            skLineSegment(sketch, "E361.trimOffspring", {"start": v(900, 5100) * mm, "end": v(1200, 5100) * mm});
            skLineSegment(sketch, "E362", {"start": v(0, 5400) * mm, "end": v(300, 5400) * mm});
            skLineSegment(sketch, "E363", {"start": v(300, 5700) * mm, "end": v(600, 5700) * mm});
            skLineSegment(sketch, "E364.trimOffspring", {"start": v(600, 5400) * mm, "end": v(900, 5400) * mm});
            skPoint(sketch, "E365.orphan", {"position": v(0, 5700) * mm});
            skLineSegment(sketch, "E366.trimOffspring", {"start": v(1200, 5100) * mm, "end": v(1200, -4546.78) * mm});
            skLineSegment(sketch, "E367.trimOffspring", {"start": v(1500, 4800) * mm, "end": v(1500, -4716.74) * mm});
            skLineSegment(sketch, "E368", {"start": v(0, 6000) * mm, "end": v(300, 6000) * mm});
            skLineSegment(sketch, "E369.trimOffspring", {"start": v(900, 5400) * mm, "end": v(900, -4376.82) * mm});
            skLineSegment(sketch, "E370.trimOffspring", {"start": v(600, 5700) * mm, "end": v(600, -4206.86) * mm});
            skLineSegment(sketch, "E371", {"start": v(300, 6425) * mm, "end": v(0, 6425) * mm});
            skLineSegment(sketch, "E372", {"start": v(0, 6425) * mm, "end": v(0, 6000) * mm});
            skLineSegment(sketch, "E373", {"start": v(2400, 3300) * mm, "end": v(2700, 3300) * mm});
            skLineSegment(sketch, "E374", {"start": v(1500, 4200) * mm, "end": v(1800, 4200) * mm});
            skLineSegment(sketch, "E375", {"start": v(1800, 4200) * mm, "end": v(1800, 3900) * mm});
            skLineSegment(sketch, "E376", {"start": v(1200, 5100) * mm, "end": v(1500, 5100) * mm});
            skLineSegment(sketch, "E377", {"start": v(1500, 5100) * mm, "end": v(1500, 4800) * mm});
            skLineSegment(sketch, "E378", {"start": v(900, 5400) * mm, "end": v(1200, 5400) * mm});
            skLineSegment(sketch, "E379", {"start": v(1200, 5400) * mm, "end": v(1200, 5100) * mm});
            skLineSegment(sketch, "E380", {"start": v(600, 5700) * mm, "end": v(900, 5700) * mm});
            skLineSegment(sketch, "E381", {"start": v(900, 5700) * mm, "end": v(900, 5400) * mm});
            skLineSegment(sketch, "E382", {"start": v(300, 6000) * mm, "end": v(600, 6000) * mm});
            skLineSegment(sketch, "E383", {"start": v(600, 6000) * mm, "end": v(600, 5700) * mm});
            skLineSegment(sketch, "E384", {"start": v(-900, -300) * mm, "end": v(-600, -300) * mm});
            skLineSegment(sketch, "E385", {"start": v(-1089, -600) * mm, "end": v(-900, -600) * mm});
            skLineSegment(sketch, "E386", {"start": v(-900, -900) * mm, "end": v(-600, -900) * mm});
            skLineSegment(sketch, "E387.trimOffspring", {"start": v(300, -300) * mm, "end": v(600, -300) * mm});
            skLineSegment(sketch, "E388.trimOffspring", {"start": v(900, -300) * mm, "end": v(1200, -300) * mm});
            skLineSegment(sketch, "E389.trimOffspring", {"start": v(1500, -300) * mm, "end": v(1800, -300) * mm});
            skLineSegment(sketch, "E390.trimOffspring", {"start": v(2100, -300) * mm, "end": v(2400, -300) * mm});
            skLineSegment(sketch, "E391.trimOffspring", {"start": v(2700, -300) * mm, "end": v(2850, -300) * mm});
            skLineSegment(sketch, "E392.trimOffspring", {"start": v(-300, -300) * mm, "end": v(0, -300) * mm});
            skPoint(sketch, "E393.orphan", {"position": v(-1089, -300) * mm});
            skLineSegment(sketch, "E394.trimOffspring", {"start": v(-600, -600) * mm, "end": v(-300, -600) * mm});
            skLineSegment(sketch, "E395.trimOffspring", {"start": v(0, -600) * mm, "end": v(300, -600) * mm});
            skLineSegment(sketch, "E396.trimOffspring", {"start": v(600, -600) * mm, "end": v(900, -600) * mm});
            skLineSegment(sketch, "E397.trimOffspring", {"start": v(1200, -600) * mm, "end": v(1500, -600) * mm});
            skLineSegment(sketch, "E398.trimOffspring", {"start": v(1800, -600) * mm, "end": v(2100, -600) * mm});
            skLineSegment(sketch, "E399.trimOffspring", {"start": v(2400, -600) * mm, "end": v(2700, -600) * mm});
            skPoint(sketch, "E400.orphan", {"position": v(-1089, -900) * mm});
            skLineSegment(sketch, "E401.trimOffspring", {"start": v(-300, -900) * mm, "end": v(0, -900) * mm});
            skLineSegment(sketch, "E402.trimOffspring", {"start": v(300, -900) * mm, "end": v(600, -900) * mm});
            skLineSegment(sketch, "E403.trimOffspring", {"start": v(900, -900) * mm, "end": v(1200, -900) * mm});
            skLineSegment(sketch, "E404.trimOffspring", {"start": v(1500, -900) * mm, "end": v(1800, -900) * mm});
            skLineSegment(sketch, "E405.trimOffspring", {"start": v(2100, -900) * mm, "end": v(2400, -900) * mm});
            skLineSegment(sketch, "E406.trimOffspring", {"start": v(2700, -900) * mm, "end": v(2850, -900) * mm});
            skLineSegment(sketch, "E407", {"start": v(-1089, -1200) * mm, "end": v(-900, -1200) * mm});
            skLineSegment(sketch, "E408", {"start": v(-900, -1500) * mm, "end": v(-600, -1500) * mm});
            skLineSegment(sketch, "E409", {"start": v(-1089, -1800) * mm, "end": v(-900, -1800) * mm});
            skLineSegment(sketch, "E410", {"start": v(-900, -2100) * mm, "end": v(-600, -2100) * mm});
            skLineSegment(sketch, "E411", {"start": v(-1089, -2400) * mm, "end": v(-900, -2400) * mm});
            skLineSegment(sketch, "E412.trimOffspring", {"start": v(-600, -1200) * mm, "end": v(-300, -1200) * mm});
            skLineSegment(sketch, "E413.trimOffspring", {"start": v(0, -1200) * mm, "end": v(300, -1200) * mm});
            skLineSegment(sketch, "E414.trimOffspring", {"start": v(600, -1200) * mm, "end": v(900, -1200) * mm});
            skLineSegment(sketch, "E415.trimOffspring", {"start": v(1200, -1200) * mm, "end": v(1500, -1200) * mm});
            skLineSegment(sketch, "E416.trimOffspring", {"start": v(1800, -1200) * mm, "end": v(2100, -1200) * mm});
            skLineSegment(sketch, "E417.trimOffspring", {"start": v(2400, -1200) * mm, "end": v(2700, -1200) * mm});
            skPoint(sketch, "E418.orphan", {"position": v(-1089, -1500) * mm});
            skLineSegment(sketch, "E419.trimOffspring", {"start": v(-300, -1500) * mm, "end": v(0, -1500) * mm});
            skLineSegment(sketch, "E420.trimOffspring", {"start": v(300, -1500) * mm, "end": v(600, -1500) * mm});
            skLineSegment(sketch, "E421.trimOffspring", {"start": v(900, -1500) * mm, "end": v(1200, -1500) * mm});
            skLineSegment(sketch, "E422.trimOffspring", {"start": v(1500, -1500) * mm, "end": v(1800, -1500) * mm});
            skLineSegment(sketch, "E423.trimOffspring", {"start": v(2100, -1500) * mm, "end": v(2400, -1500) * mm});
            skLineSegment(sketch, "E424.trimOffspring", {"start": v(2700, -1500) * mm, "end": v(2850, -1500) * mm});
            skLineSegment(sketch, "E425.trimOffspring", {"start": v(-600, -1800) * mm, "end": v(-300, -1800) * mm});
            skLineSegment(sketch, "E426.trimOffspring", {"start": v(0, -1800) * mm, "end": v(300, -1800) * mm});
            skLineSegment(sketch, "E427.trimOffspring", {"start": v(600, -1800) * mm, "end": v(900, -1800) * mm});
            skLineSegment(sketch, "E428.trimOffspring", {"start": v(1200, -1800) * mm, "end": v(1500, -1800) * mm});
            skLineSegment(sketch, "E429.trimOffspring", {"start": v(1800, -1800) * mm, "end": v(2100, -1800) * mm});
            skLineSegment(sketch, "E430.trimOffspring", {"start": v(2400, -1800) * mm, "end": v(2700, -1800) * mm});
            skPoint(sketch, "E431.orphan", {"position": v(-1089, -2100) * mm});
            skLineSegment(sketch, "E432.trimOffspring", {"start": v(-300, -2100) * mm, "end": v(0, -2100) * mm});
            skLineSegment(sketch, "E433.trimOffspring", {"start": v(300, -2100) * mm, "end": v(600, -2100) * mm});
            skLineSegment(sketch, "E434.trimOffspring", {"start": v(900, -2100) * mm, "end": v(1200, -2100) * mm});
            skLineSegment(sketch, "E435.trimOffspring", {"start": v(1500, -2100) * mm, "end": v(1800, -2100) * mm});
            skLineSegment(sketch, "E436.trimOffspring", {"start": v(2100, -2100) * mm, "end": v(2400, -2100) * mm});
            skLineSegment(sketch, "E437.trimOffspring", {"start": v(2700, -2100) * mm, "end": v(2850, -2100) * mm});
            skLineSegment(sketch, "E438.trimOffspring", {"start": v(-600, -2400) * mm, "end": v(-300, -2400) * mm});
            skLineSegment(sketch, "E439.trimOffspring", {"start": v(0, -2400) * mm, "end": v(300, -2400) * mm});
            skLineSegment(sketch, "E440.trimOffspring", {"start": v(600, -2400) * mm, "end": v(900, -2400) * mm});
            skLineSegment(sketch, "E441.trimOffspring", {"start": v(1200, -2400) * mm, "end": v(1500, -2400) * mm});
            skLineSegment(sketch, "E442.trimOffspring", {"start": v(1800, -2400) * mm, "end": v(2100, -2400) * mm});
            skLineSegment(sketch, "E443.trimOffspring", {"start": v(2400, -2400) * mm, "end": v(2700, -2400) * mm});
            skLineSegment(sketch, "E444", {"start": v(-900, -2700) * mm, "end": v(-600, -2700) * mm});
            skLineSegment(sketch, "E445", {"start": v(-1089, -3000) * mm, "end": v(-900, -3000) * mm});
            skLineSegment(sketch, "E446", {"start": v(-1000.74, -3300) * mm, "end": v(-600, -3300) * mm});
            skPoint(sketch, "E447.orphan", {"position": v(-1089, -2700) * mm});
            skLineSegment(sketch, "E448.trimOffspring", {"start": v(-300, -2700) * mm, "end": v(0, -2700) * mm});
            skLineSegment(sketch, "E449.trimOffspring", {"start": v(300, -2700) * mm, "end": v(600, -2700) * mm});
            skLineSegment(sketch, "E450.trimOffspring", {"start": v(900, -2700) * mm, "end": v(1200, -2700) * mm});
            skLineSegment(sketch, "E451.trimOffspring", {"start": v(1500, -2700) * mm, "end": v(1800, -2700) * mm});
            skLineSegment(sketch, "E452.trimOffspring", {"start": v(2100, -2700) * mm, "end": v(2400, -2700) * mm});
            skLineSegment(sketch, "E453.trimOffspring", {"start": v(2700, -2700) * mm, "end": v(2850, -2700) * mm});
            skLineSegment(sketch, "E454.trimOffspring", {"start": v(-600, -3000) * mm, "end": v(-300, -3000) * mm});
            skLineSegment(sketch, "E455.trimOffspring", {"start": v(0, -3000) * mm, "end": v(300, -3000) * mm});
            skLineSegment(sketch, "E456.trimOffspring", {"start": v(600, -3000) * mm, "end": v(900, -3000) * mm});
            skLineSegment(sketch, "E457.trimOffspring", {"start": v(1200, -3000) * mm, "end": v(1500, -3000) * mm});
            skLineSegment(sketch, "E458.trimOffspring", {"start": v(1800, -3000) * mm, "end": v(2100, -3000) * mm});
            skLineSegment(sketch, "E459.trimOffspring", {"start": v(2400, -3000) * mm, "end": v(2700, -3000) * mm});
            skLineSegment(sketch, "E460.trimOffspring", {"start": v(-300, -3300) * mm, "end": v(0, -3300) * mm});
            skLineSegment(sketch, "E461.trimOffspring", {"start": v(300, -3300) * mm, "end": v(600, -3300) * mm});
            skLineSegment(sketch, "E462.trimOffspring", {"start": v(900, -3300) * mm, "end": v(1200, -3300) * mm});
            skLineSegment(sketch, "E463.trimOffspring", {"start": v(1500, -3300) * mm, "end": v(1800, -3300) * mm});
            skLineSegment(sketch, "E464.trimOffspring", {"start": v(2100, -3300) * mm, "end": v(2400, -3300) * mm});
            skLineSegment(sketch, "E465.trimOffspring", {"start": v(2700, -3300) * mm, "end": v(2850, -3300) * mm});
            skLineSegment(sketch, "E466", {"start": v(2700, -3600) * mm, "end": v(2400, -3600) * mm});
            skLineSegment(sketch, "E467", {"start": v(300, -3900) * mm, "end": v(600, -3900) * mm});
            skLineSegment(sketch, "E468.trimOffspring", {"start": v(2100, -3600) * mm, "end": v(1800, -3600) * mm});
            skLineSegment(sketch, "E469.trimOffspring", {"start": v(1500, -3600) * mm, "end": v(1200, -3600) * mm});
            skLineSegment(sketch, "E470.trimOffspring", {"start": v(900, -3600) * mm, "end": v(600, -3600) * mm});
            skLineSegment(sketch, "E471.trimOffspring", {"start": v(300, -3600) * mm, "end": v(0, -3600) * mm});
            skLineSegment(sketch, "E472.trimOffspring", {"start": v(-300, -3600) * mm, "end": v(-471.2, -3600) * mm});
            skPoint(sketch, "E473.orphan", {"position": v(58.34, -3900) * mm});
            skLineSegment(sketch, "E474.trimOffspring", {"start": v(900, -3900) * mm, "end": v(1200, -3900) * mm});
            skLineSegment(sketch, "E475.trimOffspring", {"start": v(1500, -3900) * mm, "end": v(1800, -3900) * mm});
            skLineSegment(sketch, "E476.trimOffspring", {"start": v(2100, -3900) * mm, "end": v(2400, -3900) * mm});
            skLineSegment(sketch, "E477.trimOffspring", {"start": v(2700, -3900) * mm, "end": v(2850, -3900) * mm});
            skLineSegment(sketch, "E478", {"start": v(600, -4200) * mm, "end": v(900, -4200) * mm});
            skLineSegment(sketch, "E479.trimOffspring", {"start": v(2400, -4200) * mm, "end": v(2700, -4200) * mm});
            skLineSegment(sketch, "E480.trimOffspring", {"start": v(1800, -4200) * mm, "end": v(2100, -4200) * mm});
            skLineSegment(sketch, "E481.trimOffspring", {"start": v(1200, -4200) * mm, "end": v(1500, -4200) * mm});
            skPoint(sketch, "E482.orphan", {"position": v(587.89, -4200) * mm});
            skLineSegment(sketch, "E483", {"start": v(1117.43, -4500) * mm, "end": v(1200, -4500) * mm});
            skLineSegment(sketch, "E484.trimOffspring", {"start": v(2700, -4500) * mm, "end": v(2850, -4500) * mm});
            skLineSegment(sketch, "E485.trimOffspring", {"start": v(2100, -4500) * mm, "end": v(2400, -4500) * mm});
            skLineSegment(sketch, "E486.trimOffspring", {"start": v(1500, -4500) * mm, "end": v(1800, -4500) * mm});
            skLineSegment(sketch, "E487", {"start": v(1800, -4800) * mm, "end": v(2100, -4800) * mm});
            skLineSegment(sketch, "E488.trimOffspring", {"start": v(2400, -4800) * mm, "end": v(2700, -4800) * mm});
            skPoint(sketch, "E489.orphan", {"position": v(1646.97, -4800) * mm});
            skLineSegment(sketch, "E490", {"start": v(2176.51, -5100) * mm, "end": v(2400, -5100) * mm});
            skLineSegment(sketch, "E491.trimOffspring", {"start": v(2700, -5100) * mm, "end": v(2850, -5100) * mm});
            skSolve(sketch);
        }
        {
            var Q0;
            Q0=qCreatedBy(makeId("Top.planeOp"),FACE);
            var sketch = newSketch(context, id + "F78", { "sketchPlane" : qUnion([Q0])});
            skLineSegment(sketch, "E492", {"start": v(0, 0) * mm, "end": v(0, 6425) * mm});
            skLineSegment(sketch, "E493", {"start": v(0, 6425) * mm, "end": v(300, 6425) * mm});
            skLineSegment(sketch, "E494", {"start": v(0, 0) * mm, "end": v(-1089, 0) * mm});
            skLineSegment(sketch, "E495", {"start": v(-1089, 0) * mm, "end": v(-1089, -3250) * mm});
            skLineSegment(sketch, "E496", {"start": v(-1089, -3250) * mm, "end": v(2495, -5280.43) * mm});
            skLineSegment(sketch, "E497", {"start": v(2495, -5280.43) * mm, "end": v(2850, -5280.43) * mm});
            skLineSegment(sketch, "E498", {"start": v(2850, -5280.43) * mm, "end": v(2850, 3300) * mm});
            skLineSegment(sketch, "E499", {"start": v(2850, 3300) * mm, "end": v(2100, 3300) * mm});
            skLineSegment(sketch, "E500", {"start": v(2100, 3300) * mm, "end": v(2100, 3600) * mm});
            skLineSegment(sketch, "E501", {"start": v(2100, 3600) * mm, "end": v(1800, 3600) * mm});
            skLineSegment(sketch, "E502", {"start": v(1800, 3600) * mm, "end": v(1800, 4200) * mm});
            skLineSegment(sketch, "E503", {"start": v(1800, 4200) * mm, "end": v(1500, 4200) * mm});
            skLineSegment(sketch, "E504", {"start": v(1500, 4200) * mm, "end": v(1500, 5100) * mm});
            skLineSegment(sketch, "E505", {"start": v(1500, 5100) * mm, "end": v(1200, 5100) * mm});
            skLineSegment(sketch, "E506", {"start": v(1200, 5100) * mm, "end": v(1200, 5400) * mm});
            skLineSegment(sketch, "E507", {"start": v(1200, 5400) * mm, "end": v(900, 5400) * mm});
            skLineSegment(sketch, "E508", {"start": v(900, 5400) * mm, "end": v(900, 5700) * mm});
            skLineSegment(sketch, "E509", {"start": v(900, 5700) * mm, "end": v(600, 5700) * mm});
            skLineSegment(sketch, "E510", {"start": v(600, 5700) * mm, "end": v(600, 6000) * mm});
            skLineSegment(sketch, "E511", {"start": v(600, 6000) * mm, "end": v(300, 6000) * mm});
            skLineSegment(sketch, "E512", {"start": v(300, 6000) * mm, "end": v(300, 6425) * mm});
            skSolve(sketch);
        }
        {
            var Q0;
            Q0=qCreatedBy(id+"F75.planeOp",FACE);
            var sketch = newSketch(context, id + "F79", { "sketchPlane" : qUnion([Q0])});
            skLineSegment(sketch, "E513", {"start": v(2850, 3300) * mm, "end": v(2100, 3300) * mm});
            skLineSegment(sketch, "E514", {"start": v(2850, 3300) * mm, "end": v(2850, 3320) * mm});
            skLineSegment(sketch, "E515", {"start": v(2850, 3320) * mm, "end": v(2120, 3320) * mm});
            skLineSegment(sketch, "E516", {"start": v(2120, 3320) * mm, "end": v(2120, 3620) * mm});
            skLineSegment(sketch, "E517", {"start": v(2120, 3620) * mm, "end": v(1820, 3620) * mm});
            skLineSegment(sketch, "E518", {"start": v(1820, 3620) * mm, "end": v(1820, 4220) * mm});
            skLineSegment(sketch, "E519", {"start": v(1820, 4220) * mm, "end": v(1520, 4220) * mm});
            skLineSegment(sketch, "E520", {"start": v(1520, 4220) * mm, "end": v(1520, 5120) * mm});
            skLineSegment(sketch, "E521", {"start": v(1520, 5120) * mm, "end": v(1220, 5120) * mm});
            skLineSegment(sketch, "E522", {"start": v(1220, 5120) * mm, "end": v(1220, 5420) * mm});
            skLineSegment(sketch, "E523", {"start": v(1220, 5420) * mm, "end": v(920, 5420) * mm});
            skLineSegment(sketch, "E524", {"start": v(920, 5420) * mm, "end": v(920, 5790) * mm});
            skLineSegment(sketch, "E525", {"start": v(920, 5790) * mm, "end": v(900, 5790) * mm});
            skLineSegment(sketch, "E526", {"start": v(900, 5790) * mm, "end": v(900, 5400) * mm});
            skLineSegment(sketch, "E527", {"start": v(900, 5400) * mm, "end": v(1200, 5400) * mm});
            skLineSegment(sketch, "E528", {"start": v(1200, 5400) * mm, "end": v(1200, 5100) * mm});
            skLineSegment(sketch, "E529", {"start": v(1200, 5100) * mm, "end": v(1500, 5100) * mm});
            skLineSegment(sketch, "E530", {"start": v(1500, 5100) * mm, "end": v(1500, 4200) * mm});
            skLineSegment(sketch, "E531", {"start": v(1500, 4200) * mm, "end": v(1800, 4200) * mm});
            skLineSegment(sketch, "E532", {"start": v(1800, 4200) * mm, "end": v(1800, 3600) * mm});
            skLineSegment(sketch, "E533", {"start": v(1800, 3600) * mm, "end": v(2100, 3600) * mm});
            skLineSegment(sketch, "E534", {"start": v(2100, 3600) * mm, "end": v(2100, 3300) * mm});
            skSolve(sketch);
        }
        {
            var Q0;
            Q0 = qSketchRegion(id + "F79", true);
            extrude(context, id + "F80", {"entities" : qUnion([Q0]), "depth" : 200 * mm, "offsetDistance" : 25 * mm});
        }
        {
            var Q0;
            Q0=makeQuery(id+"F80.opExtrude","CAP_FACE",FACE,{"disambiguationData":[OSD([sQuery(id+"F79.wireOp",EDGE,"E513"),sQuery(id+"F79.wireOp",EDGE,"E514"),sQuery(id+"F79.wireOp",EDGE,"E515"),sQuery(id+"F79.wireOp",EDGE,"E516"),sQuery(id+"F79.wireOp",EDGE,"E517"),sQuery(id+"F79.wireOp",EDGE,"E518"),sQuery(id+"F79.wireOp",EDGE,"E519"),sQuery(id+"F79.wireOp",EDGE,"E520"),sQuery(id+"F79.wireOp",EDGE,"E521"),sQuery(id+"F79.wireOp",EDGE,"E522"),sQuery(id+"F79.wireOp",EDGE,"E523"),sQuery(id+"F79.wireOp",EDGE,"E524"),sQuery(id+"F79.wireOp",EDGE,"E525"),sQuery(id+"F79.wireOp",EDGE,"E526"),sQuery(id+"F79.wireOp",EDGE,"E527"),sQuery(id+"F79.wireOp",EDGE,"E528"),sQuery(id+"F79.wireOp",EDGE,"E529"),sQuery(id+"F79.wireOp",EDGE,"E530"),sQuery(id+"F79.wireOp",EDGE,"E531"),sQuery(id+"F79.wireOp",EDGE,"E532"),sQuery(id+"F79.wireOp",EDGE,"E533"),sQuery(id+"F79.wireOp",EDGE,"E534")])],"isStart":false});
            var sketch = newSketch(context, id + "F81", { "sketchPlane" : qUnion([Q0])});
            skLineSegment(sketch, "E535", {"start": v(2850, 3300) * mm, "end": v(2850, 7500) * mm});
            skLineSegment(sketch, "E536", {"start": v(2700, 3300) * mm, "end": v(2700, 7500) * mm});
            skLineSegment(sketch, "E537", {"start": v(2400, 3300) * mm, "end": v(2400, 7500) * mm});
            skLineSegment(sketch, "E538", {"start": v(2100, 3300) * mm, "end": v(2100, 7500) * mm});
            skLineSegment(sketch, "E539", {"start": v(1800, 3600) * mm, "end": v(1800, 7459.4) * mm});
            skLineSegment(sketch, "E540", {"start": v(1500, 4200) * mm, "end": v(1500, 7059.5) * mm});
            skLineSegment(sketch, "E541", {"start": v(1200, 5100) * mm, "end": v(1200, 6659.6) * mm});
            skLineSegment(sketch, "E542", {"start": v(900, 5400) * mm, "end": v(900, 6425) * mm});
            skLineSegment(sketch, "E543", {"start": v(1800, 3600) * mm, "end": v(2100, 3600) * mm});
            skLineSegment(sketch, "E544", {"start": v(1500, 4200) * mm, "end": v(2100, 4200) * mm});
            skLineSegment(sketch, "E545", {"start": v(1200, 5100) * mm, "end": v(1800, 5100) * mm});
            skLineSegment(sketch, "E546", {"start": v(900, 5400) * mm, "end": v(1500, 5400) * mm});
            skLineSegment(sketch, "E547", {"start": v(900, 5700) * mm, "end": v(1200, 5700) * mm});
            skLineSegment(sketch, "E548", {"start": v(1800, 4800) * mm, "end": v(2100, 4800) * mm});
            skLineSegment(sketch, "E549", {"start": v(2100, 3900) * mm, "end": v(2400, 3900) * mm});
            skLineSegment(sketch, "E550.trimOffspring", {"start": v(2400, 3600) * mm, "end": v(2700, 3600) * mm});
            skLineSegment(sketch, "E551.trimOffspring", {"start": v(2400, 4200) * mm, "end": v(2700, 4200) * mm});
            skLineSegment(sketch, "E552.trimOffspring", {"start": v(2700, 3900) * mm, "end": v(2850, 3900) * mm});
            skLineSegment(sketch, "E553", {"start": v(1500, 4500) * mm, "end": v(1800, 4500) * mm});
            skLineSegment(sketch, "E554.trimOffspring", {"start": v(2700, 4500) * mm, "end": v(2850, 4500) * mm});
            skLineSegment(sketch, "E555.trimOffspring", {"start": v(2100, 4500) * mm, "end": v(2400, 4500) * mm});
            skLineSegment(sketch, "E556.trimOffspring", {"start": v(2400, 4800) * mm, "end": v(2700, 4800) * mm});
            skLineSegment(sketch, "E557.trimOffspring", {"start": v(2100, 5100) * mm, "end": v(2400, 5100) * mm});
            skLineSegment(sketch, "E558.trimOffspring", {"start": v(2700, 5100) * mm, "end": v(2850, 5100) * mm});
            skLineSegment(sketch, "E559.trimOffspring", {"start": v(2400, 5400) * mm, "end": v(2700, 5400) * mm});
            skLineSegment(sketch, "E560.trimOffspring", {"start": v(1800, 5400) * mm, "end": v(2100, 5400) * mm});
            skLineSegment(sketch, "E561.trimOffspring", {"start": v(2700, 5700) * mm, "end": v(2850, 5700) * mm});
            skLineSegment(sketch, "E562.trimOffspring", {"start": v(2100, 5700) * mm, "end": v(2400, 5700) * mm});
            skLineSegment(sketch, "E563.trimOffspring", {"start": v(1500, 5700) * mm, "end": v(1800, 5700) * mm});
            skLineSegment(sketch, "E564", {"start": v(1200, 6000) * mm, "end": v(1500, 6000) * mm});
            skLineSegment(sketch, "E565", {"start": v(900, 6300) * mm, "end": v(1200, 6300) * mm});
            skPoint(sketch, "E566.orphan", {"position": v(900, 6000) * mm});
            skLineSegment(sketch, "E567.trimOffspring", {"start": v(1800, 6000) * mm, "end": v(2100, 6000) * mm});
            skLineSegment(sketch, "E568.trimOffspring", {"start": v(2400, 6000) * mm, "end": v(2700, 6000) * mm});
            skLineSegment(sketch, "E569", {"start": v(2700, 6600) * mm, "end": v(2400, 6600) * mm});
            skLineSegment(sketch, "E570.trimOffspring", {"start": v(1500, 6300) * mm, "end": v(1800, 6300) * mm});
            skLineSegment(sketch, "E571.trimOffspring", {"start": v(2100, 6300) * mm, "end": v(2400, 6300) * mm});
            skLineSegment(sketch, "E572.trimOffspring", {"start": v(2700, 6300) * mm, "end": v(2850, 6300) * mm});
            skPoint(sketch, "E573.orphan", {"position": v(2850, 6600) * mm});
            skLineSegment(sketch, "E574.trimOffspring", {"start": v(2100, 6600) * mm, "end": v(1800, 6600) * mm});
            skLineSegment(sketch, "E575.trimOffspring", {"start": v(1500, 6600) * mm, "end": v(1200, 6600) * mm});
            skLineSegment(sketch, "E576", {"start": v(2850, 6900) * mm, "end": v(2700, 6900) * mm});
            skLineSegment(sketch, "E577", {"start": v(2700, 7200) * mm, "end": v(2400, 7200) * mm});
            skLineSegment(sketch, "E578", {"start": v(2850, 7500) * mm, "end": v(2700, 7500) * mm});
            skLineSegment(sketch, "E579.trimOffspring", {"start": v(2400, 6900) * mm, "end": v(2100, 6900) * mm});
            skLineSegment(sketch, "E580.trimOffspring", {"start": v(1800, 6900) * mm, "end": v(1500, 6900) * mm});
            skLineSegment(sketch, "E581.trimOffspring", {"start": v(2100, 7200) * mm, "end": v(1800, 7200) * mm});
            skPoint(sketch, "E582.orphan", {"position": v(2850, 7200) * mm});
            skLineSegment(sketch, "E583.trimOffspring", {"start": v(2400, 7500) * mm, "end": v(2100, 7500) * mm});
            skLineSegment(sketch, "E584", {"start": v(2100, 7500) * mm, "end": v(1830.46, 7500) * mm});
            skLineSegment(sketch, "E585", {"start": v(2400, 7500) * mm, "end": v(2700, 7500) * mm});
            skSolve(sketch);
        }
        {
            var Q0;
            {var subQ0=makeQuery(id+"F80.opExtrude","CAP_EDGE",EDGE,{"disambiguationData":[OSD([sQuery(id+"F79.wireOp",EDGE,"E516")])],"isStart":false});Q0=makeQuery(id+"F81.imprint","IMPRINT",FACE,{"disambiguationData":[TD([[makeQuery(id+"F81.imprint","IMPRINT",EDGE,{"derivedFrom":subQ0}),1.0]])]});}
            var sketch = newSketch(context, id + "F82", { "sketchPlane" : qUnion([Q0])});
            skLineSegment(sketch, "E586", {"start": v(2850, 3300) * mm, "end": v(2850, 7500) * mm});
            skLineSegment(sketch, "E587", {"start": v(2850, 7500) * mm, "end": v(1830.46, 7500) * mm});
            skLineSegment(sketch, "E588", {"start": v(1830.46, 7500) * mm, "end": v(900, 6259.7) * mm});
            skLineSegment(sketch, "E589", {"start": v(900, 6259.7) * mm, "end": v(900, 5400) * mm});
            skLineSegment(sketch, "E590", {"start": v(900, 5400) * mm, "end": v(1200, 5400) * mm});
            skLineSegment(sketch, "E591", {"start": v(1200, 5400) * mm, "end": v(1200, 5100) * mm});
            skLineSegment(sketch, "E592", {"start": v(1200, 5100) * mm, "end": v(1500, 5100) * mm});
            skLineSegment(sketch, "E593", {"start": v(1500, 5100) * mm, "end": v(1500, 4200) * mm});
            skLineSegment(sketch, "E594", {"start": v(1500, 4200) * mm, "end": v(1800, 4200) * mm});
            skLineSegment(sketch, "E595", {"start": v(1800, 4200) * mm, "end": v(1800, 3600) * mm});
            skLineSegment(sketch, "E596", {"start": v(1800, 3600) * mm, "end": v(2100, 3600) * mm});
            skLineSegment(sketch, "E597", {"start": v(2100, 3600) * mm, "end": v(2100, 3300) * mm});
            skLineSegment(sketch, "E598", {"start": v(2850, 3300) * mm, "end": v(2100, 3300) * mm});
            skSolve(sketch);
        }
        {
            var Q0;
            Q0 = qSketchRegion(id + "F82", true);
            extrude(context, id + "F83", {"entities" : qUnion([Q0]), "operationType" : NewBodyOperationType.ADD, "depth" : 20 * mm, "offsetDistance" : 25 * mm});
        }
        {
            var Q0;
            Q0=qCreatedBy(makeId("Top.planeOp"),FACE);
            var sketch = newSketch(context, id + "F84", { "sketchPlane" : qUnion([Q0])});
            skLineSegment(sketch, "E599", {"start": v(0, 0) * mm, "end": v(-1089, 0) * mm});
            skLineSegment(sketch, "E600", {"start": v(-1089, 0) * mm, "end": v(-1089, -3250) * mm});
            skLineSegment(sketch, "E601", {"start": v(-1089, -3250) * mm, "end": v(2495, -5280.43) * mm});
            skLineSegment(sketch, "E602", {"start": v(2495, -5280.43) * mm, "end": v(2850, -5280.43) * mm});
            skLineSegment(sketch, "E603", {"start": v(2850, -5280.43) * mm, "end": v(2850, 3300) * mm});
            skLineSegment(sketch, "E604", {"start": v(2850, 3300) * mm, "end": v(900, 3300) * mm});
            skLineSegment(sketch, "E605", {"start": v(0, 3300) * mm, "end": v(0, 0) * mm});
            skLineSegment(sketch, "E606", {"start": v(0, 3300) * mm, "end": v(0, 5770) * mm});
            skLineSegment(sketch, "E607", {"start": v(0, 5770) * mm, "end": v(900, 5770) * mm});
            skLineSegment(sketch, "E608", {"start": v(900, 5770) * mm, "end": v(900, 3300) * mm});
            skSolve(sketch);
        }
        {
            var Q0;
            Q0 = qSketchRegion(id + "F84", true);
            extrude(context, id + "F85", {"entities" : qUnion([Q0]), "operationType" : NewBodyOperationType.ADD, "oppositeDirection" : true, "depth" : 20 * mm, "offsetDistance" : 25 * mm});
        }
        {
            var Q0;
            Q0=qCreatedBy(id+"F75.planeOp",FACE);
            var sketch = newSketch(context, id + "F86", { "sketchPlane" : qUnion([Q0])});
            skLineSegment(sketch, "E609", {"start": v(2850, 3320) * mm, "end": v(2850, 3300) * mm});
            skLineSegment(sketch, "E610", {"start": v(2850, 3300) * mm, "end": v(900, 3300) * mm});
            skLineSegment(sketch, "E611", {"start": v(900, 3300) * mm, "end": v(900, 6425) * mm});
            skLineSegment(sketch, "E612", {"start": v(900, 6425) * mm, "end": v(920, 6425) * mm});
            skLineSegment(sketch, "E613", {"start": v(920, 6425) * mm, "end": v(920, 3320) * mm});
            skLineSegment(sketch, "E614", {"start": v(920, 3320) * mm, "end": v(2850, 3320) * mm});
            skSolve(sketch);
        }
        {
            var Q0;
            Q0 = qSketchRegion(id + "F86", true);
            extrude(context, id + "F87", {"entities" : qUnion([Q0]), "depth" : 200 * mm, "offsetDistance" : 25 * mm});
        }
        {
            var Q0;
            Q0=makeQuery(id+"F87.opExtrude","CAP_FACE",FACE,{"disambiguationData":[OSD([sQuery(id+"F86.wireOp",EDGE,"E609"),sQuery(id+"F86.wireOp",EDGE,"E610"),sQuery(id+"F86.wireOp",EDGE,"E611"),sQuery(id+"F86.wireOp",EDGE,"E612"),sQuery(id+"F86.wireOp",EDGE,"E613"),sQuery(id+"F86.wireOp",EDGE,"E614")])],"isStart":false});
            var sketch = newSketch(context, id + "F88", { "sketchPlane" : qUnion([Q0])});
            skLineSegment(sketch, "E615", {"start": v(2850, 3300) * mm, "end": v(900, 3300) * mm});
            skLineSegment(sketch, "E616", {"start": v(900, 3300) * mm, "end": v(900, 6425) * mm});
            skLineSegment(sketch, "E617", {"start": v(900, 6425) * mm, "end": v(1024, 6425) * mm});
            skLineSegment(sketch, "E618", {"start": v(1024, 6425) * mm, "end": v(1830.46, 7500) * mm});
            skLineSegment(sketch, "E619", {"start": v(1830.46, 7500) * mm, "end": v(2850, 7500) * mm});
            skLineSegment(sketch, "E620", {"start": v(2850, 7500) * mm, "end": v(2850, 3300) * mm});
            skSolve(sketch);
        }
        {
            var Q0;
            Q0 = qSketchRegion(id + "F88", true);
            extrude(context, id + "F89", {"entities" : qUnion([Q0]), "operationType" : NewBodyOperationType.ADD, "depth" : 20 * mm, "offsetDistance" : 25 * mm});
        }
        {
            var Q0;
            Q0=qCreatedBy(makeId("Top.planeOp"),FACE);
            var sketch = newSketch(context, id + "F90", { "sketchPlane" : qUnion([Q0])});
            skLineSegment(sketch, "E621.bottom", {"start": v(750, -500) * mm, "end": v(850, -500) * mm});
            skLineSegment(sketch, "E621.top", {"start": v(750, -600) * mm, "end": v(850, -600) * mm});
            skLineSegment(sketch, "E621.left", {"start": v(750, -500) * mm, "end": v(750, -600) * mm});
            skLineSegment(sketch, "E621.right", {"start": v(850, -500) * mm, "end": v(850, -600) * mm});
            skLineSegment(sketch, "E622.bottom", {"start": v(1850, -500) * mm, "end": v(1950, -500) * mm});
            skLineSegment(sketch, "E622.top", {"start": v(1850, -600) * mm, "end": v(1950, -600) * mm});
            skLineSegment(sketch, "E622.left", {"start": v(1850, -500) * mm, "end": v(1850, -600) * mm});
            skLineSegment(sketch, "E622.right", {"start": v(1950, -500) * mm, "end": v(1950, -600) * mm});
            skLineSegment(sketch, "E623.bottom", {"start": v(750, -3200) * mm, "end": v(850, -3200) * mm});
            skLineSegment(sketch, "E623.top", {"start": v(750, -3300) * mm, "end": v(850, -3300) * mm});
            skLineSegment(sketch, "E623.left", {"start": v(750, -3200) * mm, "end": v(750, -3300) * mm});
            skLineSegment(sketch, "E623.right", {"start": v(850, -3200) * mm, "end": v(850, -3300) * mm});
            skLineSegment(sketch, "E624.bottom", {"start": v(1850, -3200) * mm, "end": v(1950, -3200) * mm});
            skLineSegment(sketch, "E624.top", {"start": v(1850, -3300) * mm, "end": v(1950, -3300) * mm});
            skLineSegment(sketch, "E624.left", {"start": v(1850, -3200) * mm, "end": v(1850, -3300) * mm});
            skLineSegment(sketch, "E624.right", {"start": v(1950, -3200) * mm, "end": v(1950, -3300) * mm});
            skSolve(sketch);
        }
        {
            var Q0;
            Q0 = qSketchRegion(id + "F90", true);
            extrude(context, id + "F91", {"entities" : qUnion([Q0]), "operationType" : NewBodyOperationType.ADD, "depth" : 700 * mm, "offsetDistance" : 25 * mm});
        }
        {
            var Q0;
            Q0=makeQuery(id+"F91.opExtrude","CAP_FACE",FACE,{"disambiguationData":[OSD([sQuery(id+"F90.wireOp",EDGE,"E621.bottom"),sQuery(id+"F90.wireOp",EDGE,"E621.top"),sQuery(id+"F90.wireOp",EDGE,"E621.left"),sQuery(id+"F90.wireOp",EDGE,"E621.right")])],"isStart":false});
            var sketch = newSketch(context, id + "F92", { "sketchPlane" : qUnion([Q0])});
            skLineSegment(sketch, "E625.bottom", {"start": v(750, -500) * mm, "end": v(1950, -500) * mm});
            skLineSegment(sketch, "E625.top", {"start": v(750, -3300) * mm, "end": v(1950, -3300) * mm});
            skLineSegment(sketch, "E625.left", {"start": v(750, -500) * mm, "end": v(750, -3300) * mm});
            skLineSegment(sketch, "E625.right", {"start": v(1950, -500) * mm, "end": v(1950, -3300) * mm});
            skSolve(sketch);
        }
        {
            var Q0;
            Q0 = qSketchRegion(id + "F92", true);
            extrude(context, id + "F93", {"entities" : qUnion([Q0]), "operationType" : NewBodyOperationType.ADD, "depth" : 100 * mm, "offsetDistance" : 25 * mm});
        }
        {
            var Q0;
            Q0=qCreatedBy(makeId("Top.planeOp"),FACE);
            cPlane(context, id + "F94", {"entities" : qUnion([Q0]), "cplaneType" : CPlaneType.OFFSET, "offset" : 400 * mm, "width" : 150 * mm, "height" : 150 * mm});
        }
        {
            var Q0;
            Q0=qCreatedBy(id+"F94.planeOp",FACE);
            var sketch = newSketch(context, id + "F95", { "sketchPlane" : qUnion([Q0])});
            skLineSegment(sketch, "E626.bottom", {"start": v(900, 3300) * mm, "end": v(1000, 3300) * mm});
            skLineSegment(sketch, "E626.top", {"start": v(900, 3400) * mm, "end": v(1000, 3400) * mm});
            skLineSegment(sketch, "E626.left", {"start": v(900, 3300) * mm, "end": v(900, 3400) * mm});
            skLineSegment(sketch, "E626.right", {"start": v(1000, 3300) * mm, "end": v(1000, 3400) * mm});
            skLineSegment(sketch, "E627.bottom", {"start": v(1275, 3300) * mm, "end": v(1375, 3300) * mm});
            skLineSegment(sketch, "E627.top", {"start": v(1275, 3400) * mm, "end": v(1375, 3400) * mm});
            skLineSegment(sketch, "E627.left", {"start": v(1275, 3300) * mm, "end": v(1275, 3400) * mm});
            skLineSegment(sketch, "E627.right", {"start": v(1375, 3300) * mm, "end": v(1375, 3400) * mm});
            skLineSegment(sketch, "E628.bottom", {"start": v(2900, 3300) * mm, "end": v(3000, 3300) * mm});
            skLineSegment(sketch, "E628.top", {"start": v(2900, 3400) * mm, "end": v(3000, 3400) * mm});
            skLineSegment(sketch, "E628.left", {"start": v(2900, 3300) * mm, "end": v(2900, 3400) * mm});
            skLineSegment(sketch, "E628.right", {"start": v(3000, 3300) * mm, "end": v(3000, 3400) * mm});
            skLineSegment(sketch, "E629.bottom", {"start": v(2375, 3300) * mm, "end": v(2475, 3300) * mm});
            skLineSegment(sketch, "E629.top", {"start": v(2375, 3400) * mm, "end": v(2475, 3400) * mm});
            skLineSegment(sketch, "E629.left", {"start": v(2375, 3300) * mm, "end": v(2375, 3400) * mm});
            skLineSegment(sketch, "E629.right", {"start": v(2475, 3300) * mm, "end": v(2475, 3400) * mm});
            skLineSegment(sketch, "E630.bottom", {"start": v(900, 3850) * mm, "end": v(1000, 3850) * mm});
            skLineSegment(sketch, "E630.top", {"start": v(900, 3750) * mm, "end": v(1000, 3750) * mm});
            skLineSegment(sketch, "E630.left", {"start": v(900, 3850) * mm, "end": v(900, 3750) * mm});
            skLineSegment(sketch, "E630.right", {"start": v(1000, 3850) * mm, "end": v(1000, 3750) * mm});
            skLineSegment(sketch, "E631.bottom", {"start": v(900, 4200) * mm, "end": v(1000, 4200) * mm});
            skLineSegment(sketch, "E631.top", {"start": v(900, 4300) * mm, "end": v(1000, 4300) * mm});
            skLineSegment(sketch, "E631.left", {"start": v(900, 4200) * mm, "end": v(900, 4300) * mm});
            skLineSegment(sketch, "E631.right", {"start": v(1000, 4200) * mm, "end": v(1000, 4300) * mm});
            skLineSegment(sketch, "E632.bottom", {"start": v(900, 4650) * mm, "end": v(1000, 4650) * mm});
            skLineSegment(sketch, "E632.top", {"start": v(900, 4750) * mm, "end": v(1000, 4750) * mm});
            skLineSegment(sketch, "E632.left", {"start": v(900, 4650) * mm, "end": v(900, 4750) * mm});
            skLineSegment(sketch, "E632.right", {"start": v(1000, 4650) * mm, "end": v(1000, 4750) * mm});
            skLineSegment(sketch, "E633.bottom", {"start": v(900, 5100) * mm, "end": v(1000, 5100) * mm});
            skLineSegment(sketch, "E633.top", {"start": v(900, 5200) * mm, "end": v(1000, 5200) * mm});
            skLineSegment(sketch, "E633.left", {"start": v(900, 5100) * mm, "end": v(900, 5200) * mm});
            skLineSegment(sketch, "E633.right", {"start": v(1000, 5100) * mm, "end": v(1000, 5200) * mm});
            skLineSegment(sketch, "E634.bottom", {"start": v(900, 5550) * mm, "end": v(1000, 5550) * mm});
            skLineSegment(sketch, "E634.top", {"start": v(900, 5650) * mm, "end": v(1000, 5650) * mm});
            skLineSegment(sketch, "E634.left", {"start": v(900, 5550) * mm, "end": v(900, 5650) * mm});
            skLineSegment(sketch, "E634.right", {"start": v(1000, 5550) * mm, "end": v(1000, 5650) * mm});
            skLineSegment(sketch, "E635.bottom", {"start": v(900, 6000) * mm, "end": v(1000, 6000) * mm});
            skLineSegment(sketch, "E635.top", {"start": v(900, 6100) * mm, "end": v(1000, 6100) * mm});
            skLineSegment(sketch, "E635.left", {"start": v(900, 6000) * mm, "end": v(900, 6100) * mm});
            skLineSegment(sketch, "E635.right", {"start": v(1000, 6000) * mm, "end": v(1000, 6100) * mm});
            skLineSegment(sketch, "E636.bottom", {"start": v(3000, 3750) * mm, "end": v(2900, 3750) * mm});
            skLineSegment(sketch, "E636.top", {"start": v(3000, 3850) * mm, "end": v(2900, 3850) * mm});
            skLineSegment(sketch, "E636.left", {"start": v(3000, 3750) * mm, "end": v(3000, 3850) * mm});
            skLineSegment(sketch, "E636.right", {"start": v(2900, 3750) * mm, "end": v(2900, 3850) * mm});
            skLineSegment(sketch, "E637.bottom", {"start": v(3000, 4200) * mm, "end": v(2900, 4200) * mm});
            skLineSegment(sketch, "E637.top", {"start": v(3000, 4300) * mm, "end": v(2900, 4300) * mm});
            skLineSegment(sketch, "E637.left", {"start": v(3000, 4200) * mm, "end": v(3000, 4300) * mm});
            skLineSegment(sketch, "E637.right", {"start": v(2900, 4200) * mm, "end": v(2900, 4300) * mm});
            skLineSegment(sketch, "E638.bottom", {"start": v(3000, 4650) * mm, "end": v(2900, 4650) * mm});
            skLineSegment(sketch, "E638.top", {"start": v(3000, 4750) * mm, "end": v(2900, 4750) * mm});
            skLineSegment(sketch, "E638.left", {"start": v(3000, 4650) * mm, "end": v(3000, 4750) * mm});
            skLineSegment(sketch, "E638.right", {"start": v(2900, 4650) * mm, "end": v(2900, 4750) * mm});
            skLineSegment(sketch, "E639.bottom", {"start": v(3000, 5100) * mm, "end": v(2900, 5100) * mm});
            skLineSegment(sketch, "E639.top", {"start": v(3000, 5200) * mm, "end": v(2900, 5200) * mm});
            skLineSegment(sketch, "E639.left", {"start": v(3000, 5100) * mm, "end": v(3000, 5200) * mm});
            skLineSegment(sketch, "E639.right", {"start": v(2900, 5100) * mm, "end": v(2900, 5200) * mm});
            skLineSegment(sketch, "E640.bottom", {"start": v(3000, 5550) * mm, "end": v(2900, 5550) * mm});
            skLineSegment(sketch, "E640.top", {"start": v(3000, 5650) * mm, "end": v(2900, 5650) * mm});
            skLineSegment(sketch, "E640.left", {"start": v(3000, 5550) * mm, "end": v(3000, 5650) * mm});
            skLineSegment(sketch, "E640.right", {"start": v(2900, 5550) * mm, "end": v(2900, 5650) * mm});
            skLineSegment(sketch, "E641.bottom", {"start": v(3000, 6000) * mm, "end": v(2900, 6000) * mm});
            skLineSegment(sketch, "E641.top", {"start": v(3000, 6100) * mm, "end": v(2900, 6100) * mm});
            skLineSegment(sketch, "E641.left", {"start": v(3000, 6000) * mm, "end": v(3000, 6100) * mm});
            skLineSegment(sketch, "E641.right", {"start": v(2900, 6000) * mm, "end": v(2900, 6100) * mm});
            skLineSegment(sketch, "E642.bottom", {"start": v(3000, 6450) * mm, "end": v(2900, 6450) * mm});
            skLineSegment(sketch, "E642.top", {"start": v(3000, 6550) * mm, "end": v(2900, 6550) * mm});
            skLineSegment(sketch, "E642.left", {"start": v(3000, 6450) * mm, "end": v(3000, 6550) * mm});
            skLineSegment(sketch, "E642.right", {"start": v(2900, 6450) * mm, "end": v(2900, 6550) * mm});
            skLineSegment(sketch, "E643.bottom", {"start": v(3000, 6900) * mm, "end": v(2900, 6900) * mm});
            skLineSegment(sketch, "E643.top", {"start": v(3000, 7000) * mm, "end": v(2900, 7000) * mm});
            skLineSegment(sketch, "E643.left", {"start": v(3000, 6900) * mm, "end": v(3000, 7000) * mm});
            skLineSegment(sketch, "E643.right", {"start": v(2900, 6900) * mm, "end": v(2900, 7000) * mm});
            skLineSegment(sketch, "E644.bottom", {"start": v(3000, 7350) * mm, "end": v(2900, 7350) * mm});
            skLineSegment(sketch, "E644.top", {"start": v(3000, 7450) * mm, "end": v(2900, 7450) * mm});
            skLineSegment(sketch, "E644.left", {"start": v(3000, 7350) * mm, "end": v(3000, 7450) * mm});
            skLineSegment(sketch, "E644.right", {"start": v(2900, 7350) * mm, "end": v(2900, 7450) * mm});
            skLineSegment(sketch, "E645", {"start": v(1892.95, 7450) * mm, "end": v(1892.95, 7350) * mm});
            skLineSegment(sketch, "E646", {"start": v(1892.95, 7350) * mm, "end": v(1792.95, 7350) * mm});
            skLineSegment(sketch, "E647", {"start": v(1792.95, 7350) * mm, "end": v(1792.95, 7450) * mm});
            skLineSegment(sketch, "E648", {"start": v(1792.95, 7450) * mm, "end": v(1892.95, 7450) * mm});
            skLineSegment(sketch, "E649.bottom", {"start": v(900, 6159.7) * mm, "end": v(1000, 6159.7) * mm});
            skLineSegment(sketch, "E649.top", {"start": v(900, 6259.7) * mm, "end": v(1000, 6259.7) * mm});
            skLineSegment(sketch, "E649.left", {"start": v(900, 6159.7) * mm, "end": v(900, 6259.7) * mm});
            skLineSegment(sketch, "E649.right", {"start": v(1000, 6159.7) * mm, "end": v(1000, 6259.7) * mm});
            skLineSegment(sketch, "E650.bottom", {"start": v(2071.25, 7726) * mm, "end": v(2171.25, 7726) * mm});
            skLineSegment(sketch, "E650.top", {"start": v(2071.25, 7626) * mm, "end": v(2171.25, 7626) * mm});
            skLineSegment(sketch, "E650.left", {"start": v(2071.25, 7726) * mm, "end": v(2071.25, 7626) * mm});
            skLineSegment(sketch, "E650.right", {"start": v(2171.25, 7726) * mm, "end": v(2171.25, 7626) * mm});
            skLineSegment(sketch, "E651.bottom", {"start": v(2805, 7726) * mm, "end": v(2905, 7726) * mm});
            skLineSegment(sketch, "E651.top", {"start": v(2805, 7626) * mm, "end": v(2905, 7626) * mm});
            skLineSegment(sketch, "E651.left", {"start": v(2805, 7726) * mm, "end": v(2805, 7626) * mm});
            skLineSegment(sketch, "E651.right", {"start": v(2905, 7726) * mm, "end": v(2905, 7626) * mm});
            skSolve(sketch);
        }
        {
            var Q0;
            Q0 = qSketchRegion(id + "F95", true);
            var Q1;
            Q1=makeQuery(id+"F53.opLoft","SWEPT_FACE",FACE,{"disambiguationData":[OSD([sQuery(id+"F29.wireOp",EDGE,"E152"),sQuery(id+"F29.wireOp",EDGE,"E153"),sQuery(id+"F29.wireOp",EDGE,"E154"),sQuery(id+"F31.wireOp",EDGE,"E162"),sQuery(id+"F31.wireOp",EDGE,"E163"),sQuery(id+"F31.wireOp",EDGE,"E164")])]});
            extrude(context, id + "F96", {"entities" : qUnion([Q0]), "endBound" : BoundingType.UP_TO_SURFACE, "oppositeDirection" : true, "depth" : 25 * mm, "endBoundEntityFace" : qUnion([Q1]), "offsetDistance" : 25 * mm});
        }
        {
            var Q0;
            Q0=qCreatedBy(id+"F94.planeOp",FACE);
            var sketch = newSketch(context, id + "F97", { "sketchPlane" : qUnion([Q0])});
            skLineSegment(sketch, "E652.bottom", {"start": v(1000, 3400) * mm, "end": v(1275, 3400) * mm});
            skLineSegment(sketch, "E652.top", {"start": v(1000, 3300) * mm, "end": v(1275, 3300) * mm});
            skLineSegment(sketch, "E652.left", {"start": v(1000, 3400) * mm, "end": v(1000, 3300) * mm});
            skLineSegment(sketch, "E652.right", {"start": v(1275, 3400) * mm, "end": v(1275, 3300) * mm});
            skLineSegment(sketch, "E653.bottom", {"start": v(2475, 3400) * mm, "end": v(2900, 3400) * mm});
            skLineSegment(sketch, "E653.top", {"start": v(2475, 3300) * mm, "end": v(2900, 3300) * mm});
            skLineSegment(sketch, "E653.left", {"start": v(2475, 3400) * mm, "end": v(2475, 3300) * mm});
            skLineSegment(sketch, "E653.right", {"start": v(2900, 3400) * mm, "end": v(2900, 3300) * mm});
            skLineSegment(sketch, "E654.bottom", {"start": v(1000, 3850) * mm, "end": v(2900, 3850) * mm});
            skLineSegment(sketch, "E654.top", {"start": v(1000, 3750) * mm, "end": v(2900, 3750) * mm});
            skLineSegment(sketch, "E654.left", {"start": v(1000, 3850) * mm, "end": v(1000, 3750) * mm});
            skLineSegment(sketch, "E654.right", {"start": v(2900, 3850) * mm, "end": v(2900, 3750) * mm});
            skLineSegment(sketch, "E655.bottom", {"start": v(1000, 4300) * mm, "end": v(2900, 4300) * mm});
            skLineSegment(sketch, "E655.top", {"start": v(1000, 4200) * mm, "end": v(2900, 4200) * mm});
            skLineSegment(sketch, "E655.left", {"start": v(1000, 4300) * mm, "end": v(1000, 4200) * mm});
            skLineSegment(sketch, "E655.right", {"start": v(2900, 4300) * mm, "end": v(2900, 4200) * mm});
            skLineSegment(sketch, "E656.bottom", {"start": v(1000, 4750) * mm, "end": v(2900, 4750) * mm});
            skLineSegment(sketch, "E656.top", {"start": v(1000, 4650) * mm, "end": v(2900, 4650) * mm});
            skLineSegment(sketch, "E656.left", {"start": v(1000, 4750) * mm, "end": v(1000, 4650) * mm});
            skLineSegment(sketch, "E656.right", {"start": v(2900, 4750) * mm, "end": v(2900, 4650) * mm});
            skLineSegment(sketch, "E657.bottom", {"start": v(1000, 5200) * mm, "end": v(2900, 5200) * mm});
            skLineSegment(sketch, "E657.top", {"start": v(1000, 5100) * mm, "end": v(2900, 5100) * mm});
            skLineSegment(sketch, "E657.left", {"start": v(1000, 5200) * mm, "end": v(1000, 5100) * mm});
            skLineSegment(sketch, "E657.right", {"start": v(2900, 5200) * mm, "end": v(2900, 5100) * mm});
            skLineSegment(sketch, "E658.bottom", {"start": v(1000, 5650) * mm, "end": v(2900, 5650) * mm});
            skLineSegment(sketch, "E658.top", {"start": v(1000, 5550) * mm, "end": v(2900, 5550) * mm});
            skLineSegment(sketch, "E658.left", {"start": v(1000, 5650) * mm, "end": v(1000, 5550) * mm});
            skLineSegment(sketch, "E658.right", {"start": v(2900, 5650) * mm, "end": v(2900, 5550) * mm});
            skLineSegment(sketch, "E659.bottom", {"start": v(1000, 6100) * mm, "end": v(2900, 6100) * mm});
            skLineSegment(sketch, "E659.top", {"start": v(1000, 6000) * mm, "end": v(2900, 6000) * mm});
            skLineSegment(sketch, "E659.left", {"start": v(1000, 6100) * mm, "end": v(1000, 6000) * mm});
            skLineSegment(sketch, "E659.right", {"start": v(2900, 6100) * mm, "end": v(2900, 6000) * mm});
            skLineSegment(sketch, "E660.bottom", {"start": v(1892.95, 7450) * mm, "end": v(2900, 7450) * mm});
            skLineSegment(sketch, "E660.top", {"start": v(1892.95, 7350) * mm, "end": v(2900, 7350) * mm});
            skLineSegment(sketch, "E660.left", {"start": v(1892.95, 7450) * mm, "end": v(1892.95, 7350) * mm});
            skLineSegment(sketch, "E660.right", {"start": v(2900, 7450) * mm, "end": v(2900, 7350) * mm});
            skLineSegment(sketch, "E661", {"start": v(1892.95, 7350) * mm, "end": v(1630.38, 7000) * mm});
            skLineSegment(sketch, "E662", {"start": v(1000, 6159.7) * mm, "end": v(900, 6259.7) * mm});
            skLineSegment(sketch, "E663", {"start": v(900, 6259.7) * mm, "end": v(1792.95, 7450) * mm});
            skLineSegment(sketch, "E664", {"start": v(1792.95, 7450) * mm, "end": v(1892.95, 7350) * mm});
            skLineSegment(sketch, "E665", {"start": v(2900, 7000) * mm, "end": v(2900, 6900) * mm});
            skLineSegment(sketch, "E666", {"start": v(2900, 6900) * mm, "end": v(1555.36, 6900) * mm});
            skLineSegment(sketch, "E667", {"start": v(2900, 7000) * mm, "end": v(1630.38, 7000) * mm});
            skLineSegment(sketch, "E668", {"start": v(2900, 6450) * mm, "end": v(1217.77, 6450) * mm});
            skLineSegment(sketch, "E669", {"start": v(2900, 6450) * mm, "end": v(2900, 6550) * mm});
            skLineSegment(sketch, "E670", {"start": v(2900, 6550) * mm, "end": v(1292.8, 6550) * mm});
            skLineSegment(sketch, "E671.trimOffspring", {"start": v(1217.77, 6450) * mm, "end": v(1000, 6159.7) * mm});
            skLineSegment(sketch, "E672.trimOffspring", {"start": v(1555.36, 6900) * mm, "end": v(1292.8, 6550) * mm});
            skLineSegment(sketch, "E673.bottom", {"start": v(2171.25, 7726) * mm, "end": v(2805, 7726) * mm});
            skLineSegment(sketch, "E673.top", {"start": v(2171.25, 7626) * mm, "end": v(2805, 7626) * mm});
            skLineSegment(sketch, "E673.left", {"start": v(2171.25, 7726) * mm, "end": v(2171.25, 7626) * mm});
            skLineSegment(sketch, "E673.right", {"start": v(2805, 7726) * mm, "end": v(2805, 7626) * mm});
            skSolve(sketch);
        }
        {
            var Q0;
            Q0 = qSketchRegion(id + "F97", true);
            extrude(context, id + "F98", {"entities" : qUnion([Q0]), "oppositeDirection" : true, "depth" : 100 * mm, "offsetDistance" : 25 * mm});
        }
        {
            var Q0;
            Q0=qCreatedBy(makeId("Top.planeOp"),FACE);
            cPlane(context, id + "F99", {"entities" : qUnion([Q0]), "cplaneType" : CPlaneType.OFFSET, "offset" : 200 * mm, "width" : 150 * mm, "height" : 150 * mm});
        }
    });
